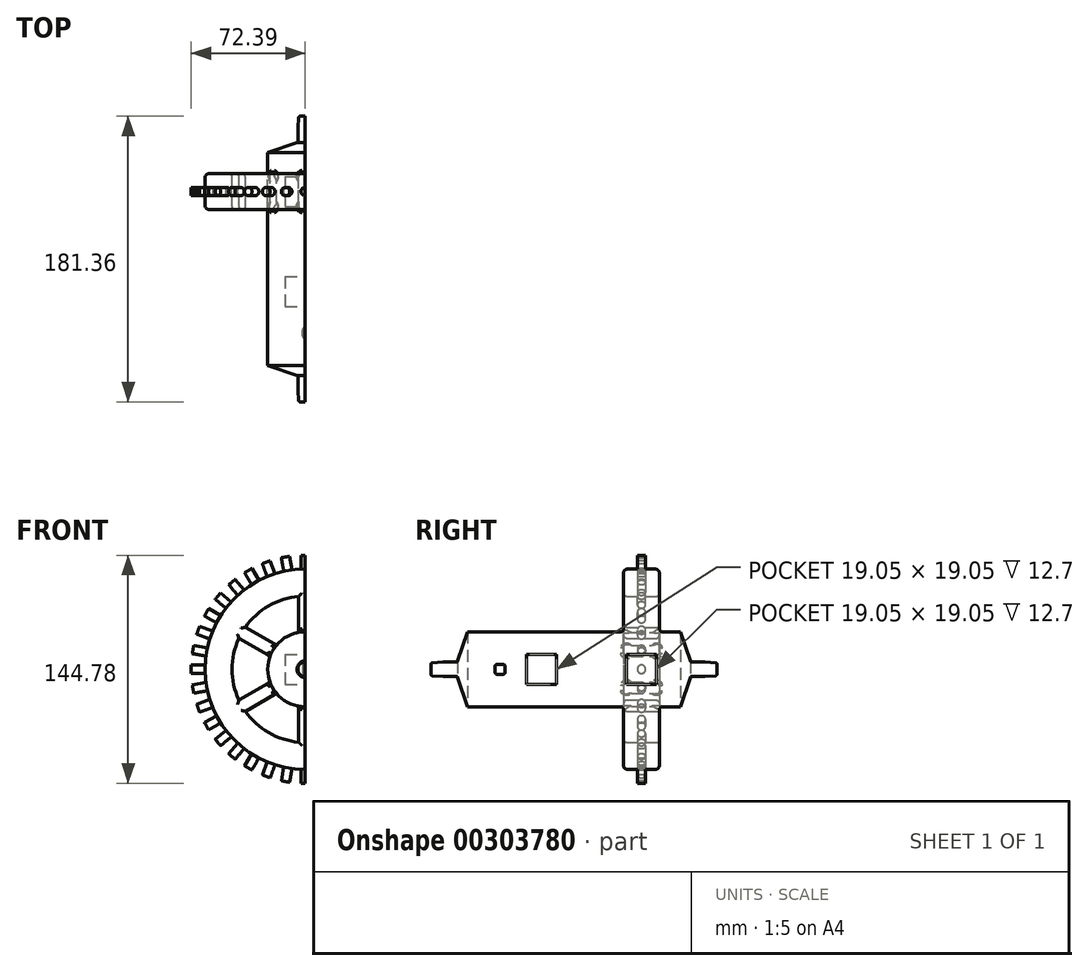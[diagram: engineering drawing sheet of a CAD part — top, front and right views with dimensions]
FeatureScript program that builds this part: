
annotation { "Feature Type Name" : "Feature", "Feature Type Description" : "" }
export const myFeature = defineFeature(function(context is Context, id is Id, definition is map)
    precondition{}
    {
        {
            var Q0;
            Q0=qCreatedBy(makeId("Front.planeOp"),FACE);
            var sketch = newSketch(context, id + "F0", { "sketchPlane" : qUnion([Q0])});
            skCircle(sketch, "E0", {"center": v(0, 0) * mm, "radius": 63.63 * mm});
            skCircle(sketch, "E1", {"center": v(0, 0) * mm, "radius": 46.48 * mm});
            skCircle(sketch, "E2", {"center": v(0, 0) * mm, "radius": 23.81 * mm});
            skCircle(sketch, "E3", {"center": v(0, 0) * mm, "radius": 4.76 * mm});
            skLineSegment(sketch, "E4.bottom", {"start": v(4.1, 47.97) * mm, "end": v(-4.1, 47.97) * mm});
            skLineSegment(sketch, "E4.top", {"start": v(4.1, 21.49) * mm, "end": v(-4.1, 21.49) * mm});
            skLineSegment(sketch, "E4.left", {"start": v(4.1, 47.97) * mm, "end": v(4.1, 21.49) * mm});
            skLineSegment(sketch, "E4.right", {"start": v(-4.1, 47.97) * mm, "end": v(-4.1, 21.49) * mm});
            skPoint(sketch, "E4.middle", {"position": v(0, 34.73) * mm});
            skPoint(sketch, "E5.1.0", {"position": v(30.08, 17.36) * mm});
            skPoint(sketch, "E5.2.0", {"position": v(30.08, -17.36) * mm});
            skLineSegment(sketch, "E5.anchor1", {"start": v(0, 0) * mm, "end": v(0, 34.73) * mm, "construction": true});
            skLineSegment(sketch, "E5.anchor2", {"start": v(0, 0) * mm, "end": v(30.08, -17.36) * mm, "construction": true});
            skLineSegment(sketch, "E6.1.0", {"start": v(43.6, 20.43) * mm, "end": v(20.66, 7.2) * mm});
            skLineSegment(sketch, "E6.2.0", {"start": v(39.5, -27.54) * mm, "end": v(16.56, -14.3) * mm});
            skLineSegment(sketch, "E6.anchor1", {"start": v(0, 0) * mm, "end": v(4.1, 21.49) * mm, "construction": true});
            skLineSegment(sketch, "E6.anchor2", {"start": v(0, 0) * mm, "end": v(16.56, -14.3) * mm, "construction": true});
            skLineSegment(sketch, "E7.1.0", {"start": v(39.5, 27.54) * mm, "end": v(16.56, 14.3) * mm});
            skLineSegment(sketch, "E7.2.0", {"start": v(43.6, -20.43) * mm, "end": v(20.66, -7.2) * mm});
            skLineSegment(sketch, "E7.anchor1", {"start": v(0, 0) * mm, "end": v(-4.1, 21.49) * mm, "construction": true});
            skLineSegment(sketch, "E7.anchor2", {"start": v(0, 0) * mm, "end": v(20.66, -7.2) * mm, "construction": true});
            skLineSegment(sketch, "E8.1.0", {"start": v(20.66, 7.2) * mm, "end": v(16.56, 14.3) * mm});
            skLineSegment(sketch, "E8.2.0", {"start": v(16.56, -14.3) * mm, "end": v(20.66, -7.2) * mm});
            skLineSegment(sketch, "E9.1.0", {"start": v(43.6, 20.43) * mm, "end": v(39.5, 27.54) * mm});
            skLineSegment(sketch, "E9.2.0", {"start": v(39.5, -27.54) * mm, "end": v(43.6, -20.43) * mm});
            skLineSegment(sketch, "E9.anchor1", {"start": v(0, 0) * mm, "end": v(-4.1, 47.97) * mm, "construction": true});
            skLineSegment(sketch, "E9.anchor2", {"start": v(0, 0) * mm, "end": v(43.6, -20.43) * mm, "construction": true});
            skLineSegment(sketch, "E10.bottom", {"start": v(4.1, -19) * mm, "end": v(-4.1, -19) * mm});
            skLineSegment(sketch, "E10.top", {"start": v(4.1, -51.61) * mm, "end": v(-4.1, -51.61) * mm});
            skLineSegment(sketch, "E10.left", {"start": v(4.1, -19) * mm, "end": v(4.1, -51.61) * mm});
            skLineSegment(sketch, "E10.right", {"start": v(-4.1, -19) * mm, "end": v(-4.1, -51.61) * mm});
            skPoint(sketch, "E10.middle", {"position": v(0, -35.3) * mm});
            skLineSegment(sketch, "E11.1.0", {"start": v(-18.5, -5.95) * mm, "end": v(-46.75, -22.25) * mm});
            skLineSegment(sketch, "E11.2.0", {"start": v(-14.4, 13.05) * mm, "end": v(-42.65, 29.36) * mm});
            skLineSegment(sketch, "E11.anchor1", {"start": v(0, 0) * mm, "end": v(-4.1, -51.61) * mm, "construction": true});
            skLineSegment(sketch, "E11.anchor2", {"start": v(0, 0) * mm, "end": v(-42.65, 29.36) * mm, "construction": true});
            skLineSegment(sketch, "E12.1.0", {"start": v(-14.4, -13.05) * mm, "end": v(-42.65, -29.36) * mm});
            skLineSegment(sketch, "E12.2.0", {"start": v(-18.5, 5.95) * mm, "end": v(-46.75, 22.25) * mm});
            skLineSegment(sketch, "E12.anchor1", {"start": v(0, 0) * mm, "end": v(4.1, -51.61) * mm, "construction": true});
            skLineSegment(sketch, "E12.anchor2", {"start": v(0, 0) * mm, "end": v(-46.75, 22.25) * mm, "construction": true});
            skLineSegment(sketch, "E13.1.0", {"start": v(-42.65, -29.36) * mm, "end": v(-46.75, -22.25) * mm});
            skLineSegment(sketch, "E13.1.1", {"start": v(-14.4, -13.05) * mm, "end": v(-18.5, -5.95) * mm});
            skLineSegment(sketch, "E13.2.0", {"start": v(-46.75, 22.25) * mm, "end": v(-42.65, 29.36) * mm});
            skLineSegment(sketch, "E13.2.1", {"start": v(-18.5, 5.95) * mm, "end": v(-14.4, 13.05) * mm});
            skSolve(sketch);
        }
        {
            var Q0;
            Q0=makeQuery(id+"F0.imprint","IMPRINT",FACE,{"disambiguationData":[TD([[makeQuery(id+"F0.imprint","IMPRINT",EDGE,{"derivedFrom":sQuery(id+"F0.wireOp",EDGE,"E0")}),1.0]])]});
            var Q1;
            {var subQ5=sQuery(id+"F0.wireOp",EDGE,"E4.bottom");Q1=makeQuery(id+"F0.imprint","IMPRINT",FACE,{"disambiguationData":[TD([[makeQuery(id+"F0.imprint","IMPRINT",EDGE,{"derivedFrom":subQ5}),1.0]])]});}
            var Q2;
            {var subQ5=sQuery(id+"F0.wireOp",EDGE,"E9.1.0");Q2=makeQuery(id+"F0.imprint","IMPRINT",FACE,{"disambiguationData":[TD([[makeQuery(id+"F0.imprint","IMPRINT",EDGE,{"derivedFrom":subQ5}),1.0]])]});}
            var Q3;
            {var subQ5=sQuery(id+"F0.wireOp",EDGE,"E9.2.0");Q3=makeQuery(id+"F0.imprint","IMPRINT",FACE,{"disambiguationData":[TD([[makeQuery(id+"F0.imprint","IMPRINT",EDGE,{"derivedFrom":subQ5}),1.0]])]});}
            var Q4;
            {var subQ5=sQuery(id+"F0.wireOp",EDGE,"E13.2.0");Q4=makeQuery(id+"F0.imprint","IMPRINT",FACE,{"disambiguationData":[TD([[makeQuery(id+"F0.imprint","IMPRINT",EDGE,{"derivedFrom":subQ5}),-1.0]])]});}
            var Q5;
            {var subQ5=sQuery(id+"F0.wireOp",EDGE,"E13.1.0");Q5=makeQuery(id+"F0.imprint","IMPRINT",FACE,{"disambiguationData":[TD([[makeQuery(id+"F0.imprint","IMPRINT",EDGE,{"derivedFrom":subQ5}),-1.0]])]});}
            var Q6;
            {var subQ5=sQuery(id+"F0.wireOp",EDGE,"E10.top");Q6=makeQuery(id+"F0.imprint","IMPRINT",FACE,{"disambiguationData":[TD([[makeQuery(id+"F0.imprint","IMPRINT",EDGE,{"derivedFrom":subQ5}),-1.0]])]});}
            extrude(context, id + "F1", {"entities" : qUnion([Q0, Q1, Q2, Q3, Q4, Q5, Q6]), "endBound" : BoundingType.SYMMETRIC, "depth" : 22.76 * mm});
        }
        {
            var Q0;
            Q0=makeQuery(id+"F1.opExtrude","CAP_EDGE",EDGE,{"disambiguationData":[OSD([sQuery(id+"F0.wireOp",EDGE,"E0")])],"isStart":false});
            var Q1;
            Q1=makeQuery(id+"F1.opExtrude","CAP_EDGE",EDGE,{"disambiguationData":[OSD([sQuery(id+"F0.wireOp",EDGE,"E0")])],"isStart":true});
            fillet(context, id + "F2", {"entities" : qUnion([Q0, Q1]), "radius" : 2.54 * mm, "tangentPropagation" : true, "allowEdgeOverflow" : false});
        }
        {
            var Q0;
            {var subQ0=sQuery(id+"F0.wireOp",EDGE,"E4.left");var subQ1=sQuery(id+"F0.wireOp",EDGE,"E1");var subQ2=makeQuery(id+"F0.imprint","INTERSECT",VERTEX,{"derivedFrom":[subQ1,subQ0]});Q0=makeQuery(id+"F0.imprint","IMPRINT",FACE,{"disambiguationData":[TD([[makeQuery(id+"F0.imprint","IMPRINT",EDGE,{"disambiguationData":[TD([[subQ2,-1.0]])],"derivedFrom":subQ1}),1.0]])]});}
            var Q1;
            {var subQ0=sQuery(id+"F0.wireOp",EDGE,"E7.1.0");var subQ1=sQuery(id+"F0.wireOp",EDGE,"E1");var subQ2=makeQuery(id+"F0.imprint","INTERSECT",VERTEX,{"derivedFrom":[subQ1,subQ0]});Q1=makeQuery(id+"F0.imprint","IMPRINT",FACE,{"disambiguationData":[TD([[makeQuery(id+"F0.imprint","IMPRINT",EDGE,{"disambiguationData":[TD([[subQ2,1.0]])],"derivedFrom":subQ1}),1.0]])]});}
            var Q2;
            {var subQ0=sQuery(id+"F0.wireOp",EDGE,"E6.2.0");var subQ1=sQuery(id+"F0.wireOp",EDGE,"E1");var subQ2=makeQuery(id+"F0.imprint","INTERSECT",VERTEX,{"derivedFrom":[subQ1,subQ0]});Q2=makeQuery(id+"F0.imprint","IMPRINT",FACE,{"disambiguationData":[TD([[makeQuery(id+"F0.imprint","IMPRINT",EDGE,{"disambiguationData":[TD([[subQ2,-1.0]])],"derivedFrom":subQ1}),1.0]])]});}
            var Q3;
            {var subQ0=sQuery(id+"F0.wireOp",EDGE,"E11.2.0");var subQ1=sQuery(id+"F0.wireOp",EDGE,"E1");var subQ2=makeQuery(id+"F0.imprint","INTERSECT",VERTEX,{"derivedFrom":[subQ1,subQ0]});Q3=makeQuery(id+"F0.imprint","IMPRINT",FACE,{"disambiguationData":[TD([[makeQuery(id+"F0.imprint","IMPRINT",EDGE,{"disambiguationData":[TD([[subQ2,-1.0]])],"derivedFrom":subQ1}),1.0]])]});}
            var Q4;
            {var subQ0=sQuery(id+"F0.wireOp",EDGE,"E11.1.0");var subQ1=sQuery(id+"F0.wireOp",EDGE,"E1");var subQ2=makeQuery(id+"F0.imprint","INTERSECT",VERTEX,{"derivedFrom":[subQ1,subQ0]});Q4=makeQuery(id+"F0.imprint","IMPRINT",FACE,{"disambiguationData":[TD([[makeQuery(id+"F0.imprint","IMPRINT",EDGE,{"disambiguationData":[TD([[subQ2,-1.0]])],"derivedFrom":subQ1}),1.0]])]});}
            var Q5;
            {var subQ0=sQuery(id+"F0.wireOp",EDGE,"E10.right");var subQ1=sQuery(id+"F0.wireOp",EDGE,"E1");var subQ2=makeQuery(id+"F0.imprint","INTERSECT",VERTEX,{"derivedFrom":[subQ1,subQ0]});Q5=makeQuery(id+"F0.imprint","IMPRINT",FACE,{"disambiguationData":[TD([[makeQuery(id+"F0.imprint","IMPRINT",EDGE,{"disambiguationData":[TD([[subQ2,-1.0]])],"derivedFrom":subQ1}),1.0]])]});}
            extrude(context, id + "F3", {"entities" : qUnion([Q0, Q1, Q2, Q3, Q4, Q5]), "operationType" : NewBodyOperationType.ADD, "endBound" : BoundingType.SYMMETRIC, "depth" : 22.76 * mm});
        }
        {
            var Q0;
            Q0=makeQuery(id+"F0.imprint","IMPRINT",FACE,{"disambiguationData":[TD([[makeQuery(id+"F0.imprint","IMPRINT",EDGE,{"derivedFrom":sQuery(id+"F0.wireOp",EDGE,"E3")}),-1.0]])]});
            var Q1;
            Q1=makeQuery(id+"F0.imprint","IMPRINT",FACE,{"disambiguationData":[TD([[makeQuery(id+"F0.imprint","IMPRINT",EDGE,{"derivedFrom":sQuery(id+"F0.wireOp",EDGE,"E3")}),1.0]])]});
            var Q2;
            {var subQ5=sQuery(id+"F0.wireOp",EDGE,"E13.1.1");Q2=makeQuery(id+"F0.imprint","IMPRINT",FACE,{"disambiguationData":[TD([[makeQuery(id+"F0.imprint","IMPRINT",EDGE,{"derivedFrom":subQ5}),1.0]])]});}
            var Q3;
            {var subQ5=sQuery(id+"F0.wireOp",EDGE,"E13.2.1");Q3=makeQuery(id+"F0.imprint","IMPRINT",FACE,{"disambiguationData":[TD([[makeQuery(id+"F0.imprint","IMPRINT",EDGE,{"derivedFrom":subQ5}),1.0]])]});}
            var Q4;
            {var subQ5=sQuery(id+"F0.wireOp",EDGE,"E4.top");Q4=makeQuery(id+"F0.imprint","IMPRINT",FACE,{"disambiguationData":[TD([[makeQuery(id+"F0.imprint","IMPRINT",EDGE,{"derivedFrom":subQ5}),-1.0]])]});}
            var Q5;
            {var subQ5=sQuery(id+"F0.wireOp",EDGE,"E8.1.0");Q5=makeQuery(id+"F0.imprint","IMPRINT",FACE,{"disambiguationData":[TD([[makeQuery(id+"F0.imprint","IMPRINT",EDGE,{"derivedFrom":subQ5}),-1.0]])]});}
            var Q6;
            {var subQ5=sQuery(id+"F0.wireOp",EDGE,"E8.2.0");Q6=makeQuery(id+"F0.imprint","IMPRINT",FACE,{"disambiguationData":[TD([[makeQuery(id+"F0.imprint","IMPRINT",EDGE,{"derivedFrom":subQ5}),-1.0]])]});}
            var Q7;
            {var subQ5=sQuery(id+"F0.wireOp",EDGE,"E10.bottom");Q7=makeQuery(id+"F0.imprint","IMPRINT",FACE,{"disambiguationData":[TD([[makeQuery(id+"F0.imprint","IMPRINT",EDGE,{"derivedFrom":subQ5}),1.0]])]});}
            extrude(context, id + "F4", {"entities" : qUnion([Q0, Q1, Q2, Q3, Q4, Q5, Q6, Q7]), "operationType" : NewBodyOperationType.ADD, "depth" : 116.78 * mm});
        }
        {
            var Q0;
            Q0=makeQuery(id+"F0.imprint","IMPRINT",FACE,{"disambiguationData":[TD([[makeQuery(id+"F0.imprint","IMPRINT",EDGE,{"derivedFrom":sQuery(id+"F0.wireOp",EDGE,"E3")}),-1.0]])]});
            var Q1;
            {var subQ5=sQuery(id+"F0.wireOp",EDGE,"E8.1.0");Q1=makeQuery(id+"F0.imprint","IMPRINT",FACE,{"disambiguationData":[TD([[makeQuery(id+"F0.imprint","IMPRINT",EDGE,{"derivedFrom":subQ5}),-1.0]])]});}
            var Q2;
            {var subQ5=sQuery(id+"F0.wireOp",EDGE,"E4.top");Q2=makeQuery(id+"F0.imprint","IMPRINT",FACE,{"disambiguationData":[TD([[makeQuery(id+"F0.imprint","IMPRINT",EDGE,{"derivedFrom":subQ5}),-1.0]])]});}
            var Q3;
            {var subQ5=sQuery(id+"F0.wireOp",EDGE,"E13.2.1");Q3=makeQuery(id+"F0.imprint","IMPRINT",FACE,{"disambiguationData":[TD([[makeQuery(id+"F0.imprint","IMPRINT",EDGE,{"derivedFrom":subQ5}),1.0]])]});}
            var Q4;
            {var subQ5=sQuery(id+"F0.wireOp",EDGE,"E13.1.1");Q4=makeQuery(id+"F0.imprint","IMPRINT",FACE,{"disambiguationData":[TD([[makeQuery(id+"F0.imprint","IMPRINT",EDGE,{"derivedFrom":subQ5}),1.0]])]});}
            var Q5;
            {var subQ5=sQuery(id+"F0.wireOp",EDGE,"E10.bottom");Q5=makeQuery(id+"F0.imprint","IMPRINT",FACE,{"disambiguationData":[TD([[makeQuery(id+"F0.imprint","IMPRINT",EDGE,{"derivedFrom":subQ5}),1.0]])]});}
            var Q6;
            {var subQ5=sQuery(id+"F0.wireOp",EDGE,"E8.2.0");Q6=makeQuery(id+"F0.imprint","IMPRINT",FACE,{"disambiguationData":[TD([[makeQuery(id+"F0.imprint","IMPRINT",EDGE,{"derivedFrom":subQ5}),-1.0]])]});}
            var Q7;
            Q7=makeQuery(id+"F0.imprint","IMPRINT",FACE,{"disambiguationData":[TD([[makeQuery(id+"F0.imprint","IMPRINT",EDGE,{"derivedFrom":sQuery(id+"F0.wireOp",EDGE,"E3")}),1.0]])]});
            extrude(context, id + "F5", {"entities" : qUnion([Q0, Q1, Q2, Q3, Q4, Q5, Q6, Q7]), "operationType" : NewBodyOperationType.ADD, "oppositeDirection" : true, "depth" : 31.05 * mm});
        }
        {
            var Q0;
            Q0=makeQuery(id+"F5.opExtrude","CAP_FACE",FACE,{"disambiguationData":[OSD([sQuery(id+"F0.wireOp",EDGE,"E2")])],"isStart":false});
            var sketch = newSketch(context, id + "F6", { "sketchPlane" : qUnion([Q0])});
            skCircle(sketch, "E14", {"center": v(0, 0) * mm, "radius": 4.7 * mm});
            skSolve(sketch);
        }
        {
            var Q0;
            Q0=makeQuery(id+"F6.imprint","IMPRINT",FACE,{"disambiguationData":[TD([[makeQuery(id+"F6.imprint","IMPRINT",EDGE,{"derivedFrom":sQuery(id+"F6.wireOp",EDGE,"E14")}),1.0]])]});
            extrude(context, id + "F7", {"entities" : qUnion([Q0]), "operationType" : NewBodyOperationType.ADD, "depth" : 16.76 * mm});
        }
        {
            var Q0;
            Q0=makeQuery(id+"F4.opExtrude","CAP_FACE",FACE,{"disambiguationData":[OSD([sQuery(id+"F0.wireOp",EDGE,"E2")])],"isStart":false});
            var sketch = newSketch(context, id + "F8", { "sketchPlane" : qUnion([Q0])});
            skCircle(sketch, "E15", {"center": v(0, 0) * mm, "radius": 4.7 * mm});
            skSolve(sketch);
        }
        {
            var Q0;
            Q0 = qSketchRegion(id + "F8", true);
            extrude(context, id + "F9", {"entities" : qUnion([Q0]), "operationType" : NewBodyOperationType.ADD, "depth" : 16.76 * mm});
        }
        {
            var Q0;
            {var subQ0=sQuery(id+"F0.wireOp",EDGE,"E2");var subQ1=sQuery(id+"F0.wireOp",EDGE,"E1");Q0=makeQuery(id+"F3.boolean.opBoolean","MERGE",FACE,{"derivedFrom":[makeQuery(id+"F1.opExtrude","CAP_FACE",FACE,{"disambiguationData":[OSD([sQuery(id+"F0.wireOp",EDGE,"E0"),subQ1])],"isStart":false}),makeQuery(id+"F3.opExtrude","CAP_FACE",FACE,{"disambiguationData":[OSD([subQ1,subQ0,sQuery(id+"F0.wireOp",EDGE,"E6.1.0"),sQuery(id+"F0.wireOp",EDGE,"E7.1.0")])],"isStart":false}),makeQuery(id+"F3.opExtrude","CAP_FACE",FACE,{"disambiguationData":[OSD([subQ1,subQ0,sQuery(id+"F0.wireOp",EDGE,"E4.left"),sQuery(id+"F0.wireOp",EDGE,"E4.right")])],"isStart":false}),makeQuery(id+"F3.opExtrude","CAP_FACE",FACE,{"disambiguationData":[OSD([subQ1,subQ0,sQuery(id+"F0.wireOp",EDGE,"E11.2.0"),sQuery(id+"F0.wireOp",EDGE,"E12.2.0")])],"isStart":false}),makeQuery(id+"F3.opExtrude","CAP_FACE",FACE,{"disambiguationData":[OSD([subQ1,subQ0,sQuery(id+"F0.wireOp",EDGE,"E11.1.0"),sQuery(id+"F0.wireOp",EDGE,"E12.1.0")])],"isStart":false}),makeQuery(id+"F3.opExtrude","CAP_FACE",FACE,{"disambiguationData":[OSD([subQ1,subQ0,sQuery(id+"F0.wireOp",EDGE,"E10.left"),sQuery(id+"F0.wireOp",EDGE,"E10.right")])],"isStart":false}),makeQuery(id+"F3.opExtrude","CAP_FACE",FACE,{"disambiguationData":[OSD([subQ1,subQ0,sQuery(id+"F0.wireOp",EDGE,"E6.2.0"),sQuery(id+"F0.wireOp",EDGE,"E7.2.0")])],"isStart":false})]});}
            var Q1;
            {var subQ0=sQuery(id+"F0.wireOp",EDGE,"E2");var subQ1=sQuery(id+"F0.wireOp",EDGE,"E1");Q1=makeQuery(id+"F4.boolean.opBoolean","MERGE",FACE,{"derivedFrom":[makeQuery(id+"F3.boolean.opBoolean","MERGE",FACE,{"derivedFrom":[makeQuery(id+"F1.opExtrude","CAP_FACE",FACE,{"disambiguationData":[OSD([sQuery(id+"F0.wireOp",EDGE,"E0"),subQ1])],"isStart":true}),makeQuery(id+"F3.opExtrude","CAP_FACE",FACE,{"disambiguationData":[OSD([subQ1,subQ0,sQuery(id+"F0.wireOp",EDGE,"E6.1.0"),sQuery(id+"F0.wireOp",EDGE,"E7.1.0")])],"isStart":true}),makeQuery(id+"F3.opExtrude","CAP_FACE",FACE,{"disambiguationData":[OSD([subQ1,subQ0,sQuery(id+"F0.wireOp",EDGE,"E4.left"),sQuery(id+"F0.wireOp",EDGE,"E4.right")])],"isStart":true}),makeQuery(id+"F3.opExtrude","CAP_FACE",FACE,{"disambiguationData":[OSD([subQ1,subQ0,sQuery(id+"F0.wireOp",EDGE,"E11.2.0"),sQuery(id+"F0.wireOp",EDGE,"E12.2.0")])],"isStart":true}),makeQuery(id+"F3.opExtrude","CAP_FACE",FACE,{"disambiguationData":[OSD([subQ1,subQ0,sQuery(id+"F0.wireOp",EDGE,"E11.1.0"),sQuery(id+"F0.wireOp",EDGE,"E12.1.0")])],"isStart":true}),makeQuery(id+"F3.opExtrude","CAP_FACE",FACE,{"disambiguationData":[OSD([subQ1,subQ0,sQuery(id+"F0.wireOp",EDGE,"E10.left"),sQuery(id+"F0.wireOp",EDGE,"E10.right")])],"isStart":true}),makeQuery(id+"F3.opExtrude","CAP_FACE",FACE,{"disambiguationData":[OSD([subQ1,subQ0,sQuery(id+"F0.wireOp",EDGE,"E6.2.0"),sQuery(id+"F0.wireOp",EDGE,"E7.2.0")])],"isStart":true})]}),makeQuery(id+"F4.opExtrude","CAP_FACE",FACE,{"disambiguationData":[OSD([subQ0])],"isStart":true})]});}
            fillet(context, id + "F10", {"entities" : qUnion([Q0, Q1]), "radius" : 1.9 * mm, "tangentPropagation" : true, "allowEdgeOverflow" : false});
        }
        {
            var Q0;
            Q0=makeQuery(id+"F4.opExtrude","CAP_EDGE",EDGE,{"disambiguationData":[OSD([sQuery(id+"F0.wireOp",EDGE,"E2")])],"isStart":false});
            var Q1;
            Q1=makeQuery(id+"F5.opExtrude","CAP_EDGE",EDGE,{"disambiguationData":[OSD([sQuery(id+"F0.wireOp",EDGE,"E2")])],"isStart":false});
            chamfer(context, id + "F11", {"entities" : qUnion([Q0, Q1]), "chamferType" : ChamferType.TWO_OFFSETS, "width1" : 18.55 * mm, "oppositeDirection" : false, "width2" : 6.35 * mm, "tangentPropagation" : true});
        }
        {
            var Q0;
            Q0=qCreatedBy(makeId("Front.planeOp"),FACE);
            var sketch = newSketch(context, id + "F12", { "sketchPlane" : qUnion([Q0])});
            skLineSegment(sketch, "E16.bottom", {"start": v(2.67, 61.09) * mm, "end": v(-2.67, 61.09) * mm});
            skLineSegment(sketch, "E16.top", {"start": v(2.67, 72.4) * mm, "end": v(-2.67, 72.4) * mm});
            skLineSegment(sketch, "E16.left", {"start": v(2.67, 61.09) * mm, "end": v(2.67, 72.4) * mm});
            skLineSegment(sketch, "E16.right", {"start": v(-2.67, 61.09) * mm, "end": v(-2.67, 72.4) * mm});
            skPoint(sketch, "E16.middle", {"position": v(0, 66.74) * mm});
            skLineSegment(sketch, "E17.1.0", {"start": v(7.98, 60.62) * mm, "end": v(9.94, 71.75) * mm});
            skLineSegment(sketch, "E17.1.1", {"start": v(15.2, 70.83) * mm, "end": v(9.94, 71.75) * mm});
            skLineSegment(sketch, "E17.1.2", {"start": v(13.23, 59.7) * mm, "end": v(15.2, 70.83) * mm});
            skLineSegment(sketch, "E17.1.3", {"start": v(13.23, 59.7) * mm, "end": v(7.98, 60.62) * mm});
            skLineSegment(sketch, "E17.2.0", {"start": v(18.39, 58.32) * mm, "end": v(22.25, 68.94) * mm});
            skLineSegment(sketch, "E17.2.1", {"start": v(27.26, 67.11) * mm, "end": v(22.25, 68.94) * mm});
            skLineSegment(sketch, "E17.2.2", {"start": v(23.4, 56.5) * mm, "end": v(27.26, 67.11) * mm});
            skLineSegment(sketch, "E17.2.3", {"start": v(23.4, 56.5) * mm, "end": v(18.39, 58.32) * mm});
            skLineSegment(sketch, "E17.3.0", {"start": v(28.23, 54.24) * mm, "end": v(33.89, 64.03) * mm});
            skLineSegment(sketch, "E17.3.1", {"start": v(38.5, 61.36) * mm, "end": v(33.89, 64.03) * mm});
            skLineSegment(sketch, "E17.3.2", {"start": v(32.85, 51.57) * mm, "end": v(38.5, 61.36) * mm});
            skLineSegment(sketch, "E17.3.3", {"start": v(32.85, 51.57) * mm, "end": v(28.23, 54.24) * mm});
            skLineSegment(sketch, "E17.4.0", {"start": v(37.22, 48.5) * mm, "end": v(44.49, 57.17) * mm});
            skLineSegment(sketch, "E17.4.1", {"start": v(48.57, 53.74) * mm, "end": v(44.49, 57.17) * mm});
            skLineSegment(sketch, "E17.4.2", {"start": v(41.3, 45.08) * mm, "end": v(48.57, 53.74) * mm});
            skLineSegment(sketch, "E17.4.3", {"start": v(41.3, 45.08) * mm, "end": v(37.22, 48.5) * mm});
            skLineSegment(sketch, "E17.5.0", {"start": v(45.08, 41.3) * mm, "end": v(53.74, 48.57) * mm});
            skLineSegment(sketch, "E17.5.1", {"start": v(57.17, 44.49) * mm, "end": v(53.74, 48.57) * mm});
            skLineSegment(sketch, "E17.5.2", {"start": v(48.5, 37.22) * mm, "end": v(57.17, 44.49) * mm});
            skLineSegment(sketch, "E17.5.3", {"start": v(48.5, 37.22) * mm, "end": v(45.08, 41.3) * mm});
            skLineSegment(sketch, "E17.6.0", {"start": v(51.57, 32.85) * mm, "end": v(61.36, 38.5) * mm});
            skLineSegment(sketch, "E17.6.1", {"start": v(64.03, 33.89) * mm, "end": v(61.36, 38.5) * mm});
            skLineSegment(sketch, "E17.6.2", {"start": v(54.24, 28.23) * mm, "end": v(64.03, 33.89) * mm});
            skLineSegment(sketch, "E17.6.3", {"start": v(54.24, 28.23) * mm, "end": v(51.57, 32.85) * mm});
            skLineSegment(sketch, "E17.7.0", {"start": v(56.5, 23.4) * mm, "end": v(67.11, 27.26) * mm});
            skLineSegment(sketch, "E17.7.1", {"start": v(68.94, 22.25) * mm, "end": v(67.11, 27.26) * mm});
            skLineSegment(sketch, "E17.7.2", {"start": v(58.32, 18.39) * mm, "end": v(68.94, 22.25) * mm});
            skLineSegment(sketch, "E17.7.3", {"start": v(58.32, 18.39) * mm, "end": v(56.5, 23.4) * mm});
            skLineSegment(sketch, "E17.8.0", {"start": v(59.7, 13.23) * mm, "end": v(70.83, 15.2) * mm});
            skLineSegment(sketch, "E17.8.1", {"start": v(71.75, 9.94) * mm, "end": v(70.83, 15.2) * mm});
            skLineSegment(sketch, "E17.8.2", {"start": v(60.62, 7.98) * mm, "end": v(71.75, 9.94) * mm});
            skLineSegment(sketch, "E17.8.3", {"start": v(60.62, 7.98) * mm, "end": v(59.7, 13.23) * mm});
            skLineSegment(sketch, "E17.9.0", {"start": v(61.09, 2.67) * mm, "end": v(72.4, 2.67) * mm});
            skLineSegment(sketch, "E17.9.1", {"start": v(72.4, -2.67) * mm, "end": v(72.4, 2.67) * mm});
            skLineSegment(sketch, "E17.9.2", {"start": v(61.09, -2.67) * mm, "end": v(72.4, -2.67) * mm});
            skLineSegment(sketch, "E17.9.3", {"start": v(61.09, -2.67) * mm, "end": v(61.09, 2.67) * mm});
            skLineSegment(sketch, "E17.10.0", {"start": v(60.62, -7.98) * mm, "end": v(71.75, -9.94) * mm});
            skLineSegment(sketch, "E17.10.1", {"start": v(70.83, -15.2) * mm, "end": v(71.75, -9.94) * mm});
            skLineSegment(sketch, "E17.10.2", {"start": v(59.7, -13.23) * mm, "end": v(70.83, -15.2) * mm});
            skLineSegment(sketch, "E17.10.3", {"start": v(59.7, -13.23) * mm, "end": v(60.62, -7.98) * mm});
            skLineSegment(sketch, "E17.11.0", {"start": v(58.32, -18.39) * mm, "end": v(68.94, -22.25) * mm});
            skLineSegment(sketch, "E17.11.1", {"start": v(67.11, -27.26) * mm, "end": v(68.94, -22.25) * mm});
            skLineSegment(sketch, "E17.11.2", {"start": v(56.5, -23.4) * mm, "end": v(67.11, -27.26) * mm});
            skLineSegment(sketch, "E17.11.3", {"start": v(56.5, -23.4) * mm, "end": v(58.32, -18.39) * mm});
            skLineSegment(sketch, "E17.12.0", {"start": v(54.24, -28.23) * mm, "end": v(64.03, -33.89) * mm});
            skLineSegment(sketch, "E17.12.1", {"start": v(61.36, -38.5) * mm, "end": v(64.03, -33.89) * mm});
            skLineSegment(sketch, "E17.12.2", {"start": v(51.57, -32.85) * mm, "end": v(61.36, -38.5) * mm});
            skLineSegment(sketch, "E17.12.3", {"start": v(51.57, -32.85) * mm, "end": v(54.24, -28.23) * mm});
            skLineSegment(sketch, "E17.13.0", {"start": v(48.5, -37.22) * mm, "end": v(57.17, -44.49) * mm});
            skLineSegment(sketch, "E17.13.1", {"start": v(53.74, -48.57) * mm, "end": v(57.17, -44.49) * mm});
            skLineSegment(sketch, "E17.13.2", {"start": v(45.08, -41.3) * mm, "end": v(53.74, -48.57) * mm});
            skLineSegment(sketch, "E17.13.3", {"start": v(45.08, -41.3) * mm, "end": v(48.5, -37.22) * mm});
            skLineSegment(sketch, "E17.14.0", {"start": v(41.3, -45.08) * mm, "end": v(48.57, -53.74) * mm});
            skLineSegment(sketch, "E17.14.1", {"start": v(44.49, -57.17) * mm, "end": v(48.57, -53.74) * mm});
            skLineSegment(sketch, "E17.14.2", {"start": v(37.22, -48.5) * mm, "end": v(44.49, -57.17) * mm});
            skLineSegment(sketch, "E17.14.3", {"start": v(37.22, -48.5) * mm, "end": v(41.3, -45.08) * mm});
            skLineSegment(sketch, "E17.15.0", {"start": v(32.85, -51.57) * mm, "end": v(38.5, -61.36) * mm});
            skLineSegment(sketch, "E17.15.1", {"start": v(33.89, -64.03) * mm, "end": v(38.5, -61.36) * mm});
            skLineSegment(sketch, "E17.15.2", {"start": v(28.23, -54.24) * mm, "end": v(33.89, -64.03) * mm});
            skLineSegment(sketch, "E17.15.3", {"start": v(28.23, -54.24) * mm, "end": v(32.85, -51.57) * mm});
            skLineSegment(sketch, "E17.16.0", {"start": v(23.4, -56.5) * mm, "end": v(27.26, -67.11) * mm});
            skLineSegment(sketch, "E17.16.1", {"start": v(22.25, -68.94) * mm, "end": v(27.26, -67.11) * mm});
            skLineSegment(sketch, "E17.16.2", {"start": v(18.39, -58.32) * mm, "end": v(22.25, -68.94) * mm});
            skLineSegment(sketch, "E17.16.3", {"start": v(18.39, -58.32) * mm, "end": v(23.4, -56.5) * mm});
            skLineSegment(sketch, "E17.17.0", {"start": v(13.23, -59.7) * mm, "end": v(15.2, -70.83) * mm});
            skLineSegment(sketch, "E17.17.1", {"start": v(9.94, -71.75) * mm, "end": v(15.2, -70.83) * mm});
            skLineSegment(sketch, "E17.17.2", {"start": v(7.98, -60.62) * mm, "end": v(9.94, -71.75) * mm});
            skLineSegment(sketch, "E17.17.3", {"start": v(7.98, -60.62) * mm, "end": v(13.23, -59.7) * mm});
            skLineSegment(sketch, "E17.18.0", {"start": v(2.67, -61.09) * mm, "end": v(2.67, -72.4) * mm});
            skLineSegment(sketch, "E17.18.1", {"start": v(-2.67, -72.4) * mm, "end": v(2.67, -72.4) * mm});
            skLineSegment(sketch, "E17.18.2", {"start": v(-2.67, -61.09) * mm, "end": v(-2.67, -72.4) * mm});
            skLineSegment(sketch, "E17.18.3", {"start": v(-2.67, -61.09) * mm, "end": v(2.67, -61.09) * mm});
            skLineSegment(sketch, "E17.19.0", {"start": v(-7.98, -60.62) * mm, "end": v(-9.94, -71.75) * mm});
            skLineSegment(sketch, "E17.19.1", {"start": v(-15.2, -70.83) * mm, "end": v(-9.94, -71.75) * mm});
            skLineSegment(sketch, "E17.19.2", {"start": v(-13.23, -59.7) * mm, "end": v(-15.2, -70.83) * mm});
            skLineSegment(sketch, "E17.19.3", {"start": v(-13.23, -59.7) * mm, "end": v(-7.98, -60.62) * mm});
            skLineSegment(sketch, "E17.20.0", {"start": v(-18.39, -58.32) * mm, "end": v(-22.25, -68.94) * mm});
            skLineSegment(sketch, "E17.20.1", {"start": v(-27.26, -67.11) * mm, "end": v(-22.25, -68.94) * mm});
            skLineSegment(sketch, "E17.20.2", {"start": v(-23.4, -56.5) * mm, "end": v(-27.26, -67.11) * mm});
            skLineSegment(sketch, "E17.20.3", {"start": v(-23.4, -56.5) * mm, "end": v(-18.39, -58.32) * mm});
            skLineSegment(sketch, "E17.21.0", {"start": v(-28.23, -54.24) * mm, "end": v(-33.89, -64.03) * mm});
            skLineSegment(sketch, "E17.21.1", {"start": v(-38.5, -61.36) * mm, "end": v(-33.89, -64.03) * mm});
            skLineSegment(sketch, "E17.21.2", {"start": v(-32.85, -51.57) * mm, "end": v(-38.5, -61.36) * mm});
            skLineSegment(sketch, "E17.21.3", {"start": v(-32.85, -51.57) * mm, "end": v(-28.23, -54.24) * mm});
            skLineSegment(sketch, "E17.22.0", {"start": v(-37.22, -48.5) * mm, "end": v(-44.49, -57.17) * mm});
            skLineSegment(sketch, "E17.22.1", {"start": v(-48.57, -53.74) * mm, "end": v(-44.49, -57.17) * mm});
            skLineSegment(sketch, "E17.22.2", {"start": v(-41.3, -45.08) * mm, "end": v(-48.57, -53.74) * mm});
            skLineSegment(sketch, "E17.22.3", {"start": v(-41.3, -45.08) * mm, "end": v(-37.22, -48.5) * mm});
            skLineSegment(sketch, "E17.23.0", {"start": v(-45.08, -41.3) * mm, "end": v(-53.74, -48.57) * mm});
            skLineSegment(sketch, "E17.23.1", {"start": v(-57.17, -44.49) * mm, "end": v(-53.74, -48.57) * mm});
            skLineSegment(sketch, "E17.23.2", {"start": v(-48.5, -37.22) * mm, "end": v(-57.17, -44.49) * mm});
            skLineSegment(sketch, "E17.23.3", {"start": v(-48.5, -37.22) * mm, "end": v(-45.08, -41.3) * mm});
            skLineSegment(sketch, "E17.24.0", {"start": v(-51.57, -32.85) * mm, "end": v(-61.36, -38.5) * mm});
            skLineSegment(sketch, "E17.24.1", {"start": v(-64.03, -33.89) * mm, "end": v(-61.36, -38.5) * mm});
            skLineSegment(sketch, "E17.24.2", {"start": v(-54.24, -28.23) * mm, "end": v(-64.03, -33.89) * mm});
            skLineSegment(sketch, "E17.24.3", {"start": v(-54.24, -28.23) * mm, "end": v(-51.57, -32.85) * mm});
            skLineSegment(sketch, "E17.25.0", {"start": v(-56.5, -23.4) * mm, "end": v(-67.11, -27.26) * mm});
            skLineSegment(sketch, "E17.25.1", {"start": v(-68.94, -22.25) * mm, "end": v(-67.11, -27.26) * mm});
            skLineSegment(sketch, "E17.25.2", {"start": v(-58.32, -18.39) * mm, "end": v(-68.94, -22.25) * mm});
            skLineSegment(sketch, "E17.25.3", {"start": v(-58.32, -18.39) * mm, "end": v(-56.5, -23.4) * mm});
            skLineSegment(sketch, "E17.26.0", {"start": v(-59.7, -13.23) * mm, "end": v(-70.83, -15.2) * mm});
            skLineSegment(sketch, "E17.26.1", {"start": v(-71.75, -9.94) * mm, "end": v(-70.83, -15.2) * mm});
            skLineSegment(sketch, "E17.26.2", {"start": v(-60.62, -7.98) * mm, "end": v(-71.75, -9.94) * mm});
            skLineSegment(sketch, "E17.26.3", {"start": v(-60.62, -7.98) * mm, "end": v(-59.7, -13.23) * mm});
            skLineSegment(sketch, "E17.27.0", {"start": v(-61.09, -2.67) * mm, "end": v(-72.4, -2.67) * mm});
            skLineSegment(sketch, "E17.27.1", {"start": v(-72.4, 2.67) * mm, "end": v(-72.4, -2.67) * mm});
            skLineSegment(sketch, "E17.27.2", {"start": v(-61.09, 2.67) * mm, "end": v(-72.4, 2.67) * mm});
            skLineSegment(sketch, "E17.27.3", {"start": v(-61.09, 2.67) * mm, "end": v(-61.09, -2.67) * mm});
            skLineSegment(sketch, "E17.28.0", {"start": v(-60.62, 7.98) * mm, "end": v(-71.75, 9.94) * mm});
            skLineSegment(sketch, "E17.28.1", {"start": v(-70.83, 15.2) * mm, "end": v(-71.75, 9.94) * mm});
            skLineSegment(sketch, "E17.28.2", {"start": v(-59.7, 13.23) * mm, "end": v(-70.83, 15.2) * mm});
            skLineSegment(sketch, "E17.28.3", {"start": v(-59.7, 13.23) * mm, "end": v(-60.62, 7.98) * mm});
            skLineSegment(sketch, "E17.29.0", {"start": v(-58.32, 18.39) * mm, "end": v(-68.94, 22.25) * mm});
            skLineSegment(sketch, "E17.29.1", {"start": v(-67.11, 27.26) * mm, "end": v(-68.94, 22.25) * mm});
            skLineSegment(sketch, "E17.29.2", {"start": v(-56.5, 23.4) * mm, "end": v(-67.11, 27.26) * mm});
            skLineSegment(sketch, "E17.29.3", {"start": v(-56.5, 23.4) * mm, "end": v(-58.32, 18.39) * mm});
            skLineSegment(sketch, "E17.30.0", {"start": v(-54.24, 28.23) * mm, "end": v(-64.03, 33.89) * mm});
            skLineSegment(sketch, "E17.30.1", {"start": v(-61.36, 38.5) * mm, "end": v(-64.03, 33.89) * mm});
            skLineSegment(sketch, "E17.30.2", {"start": v(-51.57, 32.85) * mm, "end": v(-61.36, 38.5) * mm});
            skLineSegment(sketch, "E17.30.3", {"start": v(-51.57, 32.85) * mm, "end": v(-54.24, 28.23) * mm});
            skLineSegment(sketch, "E17.31.0", {"start": v(-48.5, 37.22) * mm, "end": v(-57.17, 44.49) * mm});
            skLineSegment(sketch, "E17.31.1", {"start": v(-53.74, 48.57) * mm, "end": v(-57.17, 44.49) * mm});
            skLineSegment(sketch, "E17.31.2", {"start": v(-45.08, 41.3) * mm, "end": v(-53.74, 48.57) * mm});
            skLineSegment(sketch, "E17.31.3", {"start": v(-45.08, 41.3) * mm, "end": v(-48.5, 37.22) * mm});
            skLineSegment(sketch, "E17.32.0", {"start": v(-41.3, 45.08) * mm, "end": v(-48.57, 53.74) * mm});
            skLineSegment(sketch, "E17.32.1", {"start": v(-44.49, 57.17) * mm, "end": v(-48.57, 53.74) * mm});
            skLineSegment(sketch, "E17.32.2", {"start": v(-37.22, 48.5) * mm, "end": v(-44.49, 57.17) * mm});
            skLineSegment(sketch, "E17.32.3", {"start": v(-37.22, 48.5) * mm, "end": v(-41.3, 45.08) * mm});
            skLineSegment(sketch, "E17.33.0", {"start": v(-32.85, 51.57) * mm, "end": v(-38.5, 61.36) * mm});
            skLineSegment(sketch, "E17.33.1", {"start": v(-33.89, 64.03) * mm, "end": v(-38.5, 61.36) * mm});
            skLineSegment(sketch, "E17.33.2", {"start": v(-28.23, 54.24) * mm, "end": v(-33.89, 64.03) * mm});
            skLineSegment(sketch, "E17.33.3", {"start": v(-28.23, 54.24) * mm, "end": v(-32.85, 51.57) * mm});
            skLineSegment(sketch, "E17.34.0", {"start": v(-23.4, 56.5) * mm, "end": v(-27.26, 67.11) * mm});
            skLineSegment(sketch, "E17.34.1", {"start": v(-22.25, 68.94) * mm, "end": v(-27.26, 67.11) * mm});
            skLineSegment(sketch, "E17.34.2", {"start": v(-18.39, 58.32) * mm, "end": v(-22.25, 68.94) * mm});
            skLineSegment(sketch, "E17.34.3", {"start": v(-18.39, 58.32) * mm, "end": v(-23.4, 56.5) * mm});
            skLineSegment(sketch, "E17.35.0", {"start": v(-13.23, 59.7) * mm, "end": v(-15.2, 70.83) * mm});
            skLineSegment(sketch, "E17.35.1", {"start": v(-9.94, 71.75) * mm, "end": v(-15.2, 70.83) * mm});
            skLineSegment(sketch, "E17.35.2", {"start": v(-7.98, 60.62) * mm, "end": v(-9.94, 71.75) * mm});
            skLineSegment(sketch, "E17.35.3", {"start": v(-7.98, 60.62) * mm, "end": v(-13.23, 59.7) * mm});
            skPoint(sketch, "E17.center", {"position": v(0, 0) * mm});
            skLineSegment(sketch, "E17.anchor1", {"start": v(0, 0) * mm, "end": v(-2.67, 61.09) * mm, "construction": true});
            skLineSegment(sketch, "E17.anchor2", {"start": v(0, 0) * mm, "end": v(-13.23, 59.7) * mm, "construction": true});
            skSolve(sketch);
        }
        {
            var Q0;
            Q0=makeQuery(id+"F12.imprint","IMPRINT",FACE,{"disambiguationData":[TD([[makeQuery(id+"F12.imprint","IMPRINT",EDGE,{"derivedFrom":sQuery(id+"F12.wireOp",EDGE,"E17.1.0")}),-1.0]])]});
            var Q1;
            Q1=makeQuery(id+"F12.imprint","IMPRINT",FACE,{"disambiguationData":[TD([[makeQuery(id+"F12.imprint","IMPRINT",EDGE,{"derivedFrom":sQuery(id+"F12.wireOp",EDGE,"E16.bottom")}),-1.0]])]});
            var Q2;
            Q2=makeQuery(id+"F12.imprint","IMPRINT",FACE,{"disambiguationData":[TD([[makeQuery(id+"F12.imprint","IMPRINT",EDGE,{"derivedFrom":sQuery(id+"F12.wireOp",EDGE,"E17.2.0")}),-1.0]])]});
            var Q3;
            Q3=makeQuery(id+"F12.imprint","IMPRINT",FACE,{"disambiguationData":[TD([[makeQuery(id+"F12.imprint","IMPRINT",EDGE,{"derivedFrom":sQuery(id+"F12.wireOp",EDGE,"E17.3.0")}),-1.0]])]});
            var Q4;
            Q4=makeQuery(id+"F12.imprint","IMPRINT",FACE,{"disambiguationData":[TD([[makeQuery(id+"F12.imprint","IMPRINT",EDGE,{"derivedFrom":sQuery(id+"F12.wireOp",EDGE,"E17.4.0")}),-1.0]])]});
            var Q5;
            Q5=makeQuery(id+"F12.imprint","IMPRINT",FACE,{"disambiguationData":[TD([[makeQuery(id+"F12.imprint","IMPRINT",EDGE,{"derivedFrom":sQuery(id+"F12.wireOp",EDGE,"E17.5.0")}),-1.0]])]});
            var Q6;
            Q6=makeQuery(id+"F12.imprint","IMPRINT",FACE,{"disambiguationData":[TD([[makeQuery(id+"F12.imprint","IMPRINT",EDGE,{"derivedFrom":sQuery(id+"F12.wireOp",EDGE,"E17.6.0")}),-1.0]])]});
            var Q7;
            Q7=makeQuery(id+"F12.imprint","IMPRINT",FACE,{"disambiguationData":[TD([[makeQuery(id+"F12.imprint","IMPRINT",EDGE,{"derivedFrom":sQuery(id+"F12.wireOp",EDGE,"E17.7.0")}),-1.0]])]});
            var Q8;
            Q8=makeQuery(id+"F12.imprint","IMPRINT",FACE,{"disambiguationData":[TD([[makeQuery(id+"F12.imprint","IMPRINT",EDGE,{"derivedFrom":sQuery(id+"F12.wireOp",EDGE,"E17.8.0")}),-1.0]])]});
            var Q9;
            Q9=makeQuery(id+"F12.imprint","IMPRINT",FACE,{"disambiguationData":[TD([[makeQuery(id+"F12.imprint","IMPRINT",EDGE,{"derivedFrom":sQuery(id+"F12.wireOp",EDGE,"E17.9.0")}),-1.0]])]});
            var Q10;
            Q10=makeQuery(id+"F12.imprint","IMPRINT",FACE,{"disambiguationData":[TD([[makeQuery(id+"F12.imprint","IMPRINT",EDGE,{"derivedFrom":sQuery(id+"F12.wireOp",EDGE,"E17.10.0")}),-1.0]])]});
            var Q11;
            Q11=makeQuery(id+"F12.imprint","IMPRINT",FACE,{"disambiguationData":[TD([[makeQuery(id+"F12.imprint","IMPRINT",EDGE,{"derivedFrom":sQuery(id+"F12.wireOp",EDGE,"E17.11.0")}),-1.0]])]});
            var Q12;
            Q12=makeQuery(id+"F12.imprint","IMPRINT",FACE,{"disambiguationData":[TD([[makeQuery(id+"F12.imprint","IMPRINT",EDGE,{"derivedFrom":sQuery(id+"F12.wireOp",EDGE,"E17.12.0")}),-1.0]])]});
            var Q13;
            Q13=makeQuery(id+"F12.imprint","IMPRINT",FACE,{"disambiguationData":[TD([[makeQuery(id+"F12.imprint","IMPRINT",EDGE,{"derivedFrom":sQuery(id+"F12.wireOp",EDGE,"E17.13.0")}),-1.0]])]});
            var Q14;
            Q14=makeQuery(id+"F12.imprint","IMPRINT",FACE,{"disambiguationData":[TD([[makeQuery(id+"F12.imprint","IMPRINT",EDGE,{"derivedFrom":sQuery(id+"F12.wireOp",EDGE,"E17.14.0")}),-1.0]])]});
            var Q15;
            Q15=makeQuery(id+"F12.imprint","IMPRINT",FACE,{"disambiguationData":[TD([[makeQuery(id+"F12.imprint","IMPRINT",EDGE,{"derivedFrom":sQuery(id+"F12.wireOp",EDGE,"E17.15.0")}),-1.0]])]});
            var Q16;
            Q16=makeQuery(id+"F12.imprint","IMPRINT",FACE,{"disambiguationData":[TD([[makeQuery(id+"F12.imprint","IMPRINT",EDGE,{"derivedFrom":sQuery(id+"F12.wireOp",EDGE,"E17.16.0")}),-1.0]])]});
            var Q17;
            Q17=makeQuery(id+"F12.imprint","IMPRINT",FACE,{"disambiguationData":[TD([[makeQuery(id+"F12.imprint","IMPRINT",EDGE,{"derivedFrom":sQuery(id+"F12.wireOp",EDGE,"E17.17.0")}),-1.0]])]});
            var Q18;
            Q18=makeQuery(id+"F12.imprint","IMPRINT",FACE,{"disambiguationData":[TD([[makeQuery(id+"F12.imprint","IMPRINT",EDGE,{"derivedFrom":sQuery(id+"F12.wireOp",EDGE,"E17.18.0")}),-1.0]])]});
            var Q19;
            Q19=makeQuery(id+"F12.imprint","IMPRINT",FACE,{"disambiguationData":[TD([[makeQuery(id+"F12.imprint","IMPRINT",EDGE,{"derivedFrom":sQuery(id+"F12.wireOp",EDGE,"E17.19.0")}),-1.0]])]});
            var Q20;
            Q20=makeQuery(id+"F12.imprint","IMPRINT",FACE,{"disambiguationData":[TD([[makeQuery(id+"F12.imprint","IMPRINT",EDGE,{"derivedFrom":sQuery(id+"F12.wireOp",EDGE,"E17.20.0")}),-1.0]])]});
            var Q21;
            Q21=makeQuery(id+"F12.imprint","IMPRINT",FACE,{"disambiguationData":[TD([[makeQuery(id+"F12.imprint","IMPRINT",EDGE,{"derivedFrom":sQuery(id+"F12.wireOp",EDGE,"E17.21.0")}),-1.0]])]});
            var Q22;
            Q22=makeQuery(id+"F12.imprint","IMPRINT",FACE,{"disambiguationData":[TD([[makeQuery(id+"F12.imprint","IMPRINT",EDGE,{"derivedFrom":sQuery(id+"F12.wireOp",EDGE,"E17.22.0")}),-1.0]])]});
            var Q23;
            Q23=makeQuery(id+"F12.imprint","IMPRINT",FACE,{"disambiguationData":[TD([[makeQuery(id+"F12.imprint","IMPRINT",EDGE,{"derivedFrom":sQuery(id+"F12.wireOp",EDGE,"E17.23.0")}),-1.0]])]});
            var Q24;
            Q24=makeQuery(id+"F12.imprint","IMPRINT",FACE,{"disambiguationData":[TD([[makeQuery(id+"F12.imprint","IMPRINT",EDGE,{"derivedFrom":sQuery(id+"F12.wireOp",EDGE,"E17.24.0")}),-1.0]])]});
            var Q25;
            Q25=makeQuery(id+"F12.imprint","IMPRINT",FACE,{"disambiguationData":[TD([[makeQuery(id+"F12.imprint","IMPRINT",EDGE,{"derivedFrom":sQuery(id+"F12.wireOp",EDGE,"E17.25.0")}),-1.0]])]});
            var Q26;
            Q26=makeQuery(id+"F12.imprint","IMPRINT",FACE,{"disambiguationData":[TD([[makeQuery(id+"F12.imprint","IMPRINT",EDGE,{"derivedFrom":sQuery(id+"F12.wireOp",EDGE,"E17.26.0")}),-1.0]])]});
            var Q27;
            Q27=makeQuery(id+"F12.imprint","IMPRINT",FACE,{"disambiguationData":[TD([[makeQuery(id+"F12.imprint","IMPRINT",EDGE,{"derivedFrom":sQuery(id+"F12.wireOp",EDGE,"E17.27.0")}),-1.0]])]});
            var Q28;
            Q28=makeQuery(id+"F12.imprint","IMPRINT",FACE,{"disambiguationData":[TD([[makeQuery(id+"F12.imprint","IMPRINT",EDGE,{"derivedFrom":sQuery(id+"F12.wireOp",EDGE,"E17.28.0")}),-1.0]])]});
            var Q29;
            Q29=makeQuery(id+"F12.imprint","IMPRINT",FACE,{"disambiguationData":[TD([[makeQuery(id+"F12.imprint","IMPRINT",EDGE,{"derivedFrom":sQuery(id+"F12.wireOp",EDGE,"E17.29.0")}),-1.0]])]});
            var Q30;
            Q30=makeQuery(id+"F12.imprint","IMPRINT",FACE,{"disambiguationData":[TD([[makeQuery(id+"F12.imprint","IMPRINT",EDGE,{"derivedFrom":sQuery(id+"F12.wireOp",EDGE,"E17.30.0")}),-1.0]])]});
            var Q31;
            Q31=makeQuery(id+"F12.imprint","IMPRINT",FACE,{"disambiguationData":[TD([[makeQuery(id+"F12.imprint","IMPRINT",EDGE,{"derivedFrom":sQuery(id+"F12.wireOp",EDGE,"E17.31.0")}),-1.0]])]});
            var Q32;
            Q32=makeQuery(id+"F12.imprint","IMPRINT",FACE,{"disambiguationData":[TD([[makeQuery(id+"F12.imprint","IMPRINT",EDGE,{"derivedFrom":sQuery(id+"F12.wireOp",EDGE,"E17.32.0")}),-1.0]])]});
            var Q33;
            Q33=makeQuery(id+"F12.imprint","IMPRINT",FACE,{"disambiguationData":[TD([[makeQuery(id+"F12.imprint","IMPRINT",EDGE,{"derivedFrom":sQuery(id+"F12.wireOp",EDGE,"E17.33.0")}),-1.0]])]});
            var Q34;
            Q34=makeQuery(id+"F12.imprint","IMPRINT",FACE,{"disambiguationData":[TD([[makeQuery(id+"F12.imprint","IMPRINT",EDGE,{"derivedFrom":sQuery(id+"F12.wireOp",EDGE,"E17.34.0")}),-1.0]])]});
            var Q35;
            Q35=makeQuery(id+"F12.imprint","IMPRINT",FACE,{"disambiguationData":[TD([[makeQuery(id+"F12.imprint","IMPRINT",EDGE,{"derivedFrom":sQuery(id+"F12.wireOp",EDGE,"E17.35.0")}),-1.0]])]});
            extrude(context, id + "F13", {"entities" : qUnion([Q0, Q1, Q2, Q3, Q4, Q5, Q6, Q7, Q8, Q9, Q10, Q11, Q12, Q13, Q14, Q15, Q16, Q17, Q18, Q19, Q20, Q21, Q22, Q23, Q24, Q25, Q26, Q27, Q28, Q29, Q30, Q31, Q32, Q33, Q34, Q35]), "operationType" : NewBodyOperationType.ADD, "endBound" : BoundingType.SYMMETRIC, "depth" : 5.33 * mm});
        }
        {
            var Q0;
            Q0=makeQuery(id+"F13.opExtrude","CAP_EDGE",EDGE,{"disambiguationData":[OSD([sQuery(id+"F12.wireOp",EDGE,"E17.35.2")])],"isStart":false});
            var Q1;
            Q1=makeQuery(id+"F13.opExtrude","CAP_EDGE",EDGE,{"disambiguationData":[OSD([sQuery(id+"F12.wireOp",EDGE,"E17.35.0")])],"isStart":false});
            var Q2;
            Q2=makeQuery(id+"F13.opExtrude","CAP_EDGE",EDGE,{"disambiguationData":[OSD([sQuery(id+"F12.wireOp",EDGE,"E16.right")])],"isStart":false});
            var Q3;
            Q3=makeQuery(id+"F13.opExtrude","CAP_EDGE",EDGE,{"disambiguationData":[OSD([sQuery(id+"F12.wireOp",EDGE,"E16.left")])],"isStart":false});
            var Q4;
            Q4=makeQuery(id+"F13.opExtrude","CAP_EDGE",EDGE,{"disambiguationData":[OSD([sQuery(id+"F12.wireOp",EDGE,"E16.right")])],"isStart":true});
            var Q5;
            Q5=makeQuery(id+"F13.opExtrude","CAP_EDGE",EDGE,{"disambiguationData":[OSD([sQuery(id+"F12.wireOp",EDGE,"E17.35.0")])],"isStart":true});
            var Q6;
            Q6=makeQuery(id+"F13.opExtrude","CAP_EDGE",EDGE,{"disambiguationData":[OSD([sQuery(id+"F12.wireOp",EDGE,"E16.left")])],"isStart":true});
            var Q7;
            Q7=makeQuery(id+"F13.opExtrude","CAP_EDGE",EDGE,{"disambiguationData":[OSD([sQuery(id+"F12.wireOp",EDGE,"E17.35.2")])],"isStart":true});
            var Q8;
            Q8=makeQuery(id+"F13.opExtrude","CAP_EDGE",EDGE,{"disambiguationData":[OSD([sQuery(id+"F12.wireOp",EDGE,"E17.34.2")])],"isStart":false});
            var Q9;
            Q9=makeQuery(id+"F13.opExtrude","CAP_EDGE",EDGE,{"disambiguationData":[OSD([sQuery(id+"F12.wireOp",EDGE,"E17.34.2")])],"isStart":true});
            var Q10;
            Q10=makeQuery(id+"F13.opExtrude","CAP_EDGE",EDGE,{"disambiguationData":[OSD([sQuery(id+"F12.wireOp",EDGE,"E17.34.0")])],"isStart":false});
            var Q11;
            Q11=makeQuery(id+"F13.opExtrude","CAP_EDGE",EDGE,{"disambiguationData":[OSD([sQuery(id+"F12.wireOp",EDGE,"E17.33.2")])],"isStart":false});
            var Q12;
            Q12=makeQuery(id+"F13.opExtrude","CAP_EDGE",EDGE,{"disambiguationData":[OSD([sQuery(id+"F12.wireOp",EDGE,"E17.33.2")])],"isStart":true});
            var Q13;
            Q13=makeQuery(id+"F13.opExtrude","CAP_EDGE",EDGE,{"disambiguationData":[OSD([sQuery(id+"F12.wireOp",EDGE,"E17.33.0")])],"isStart":false});
            var Q14;
            Q14=makeQuery(id+"F13.opExtrude","CAP_EDGE",EDGE,{"disambiguationData":[OSD([sQuery(id+"F12.wireOp",EDGE,"E17.32.2")])],"isStart":false});
            var Q15;
            Q15=makeQuery(id+"F13.opExtrude","CAP_EDGE",EDGE,{"disambiguationData":[OSD([sQuery(id+"F12.wireOp",EDGE,"E17.32.2")])],"isStart":true});
            var Q16;
            Q16=makeQuery(id+"F13.opExtrude","CAP_EDGE",EDGE,{"disambiguationData":[OSD([sQuery(id+"F12.wireOp",EDGE,"E17.32.0")])],"isStart":false});
            var Q17;
            Q17=makeQuery(id+"F13.opExtrude","CAP_EDGE",EDGE,{"disambiguationData":[OSD([sQuery(id+"F12.wireOp",EDGE,"E17.31.2")])],"isStart":false});
            var Q18;
            Q18=makeQuery(id+"F13.opExtrude","CAP_EDGE",EDGE,{"disambiguationData":[OSD([sQuery(id+"F12.wireOp",EDGE,"E17.31.0")])],"isStart":false});
            var Q19;
            Q19=makeQuery(id+"F13.opExtrude","CAP_EDGE",EDGE,{"disambiguationData":[OSD([sQuery(id+"F12.wireOp",EDGE,"E17.30.2")])],"isStart":false});
            var Q20;
            Q20=makeQuery(id+"F13.opExtrude","CAP_EDGE",EDGE,{"disambiguationData":[OSD([sQuery(id+"F12.wireOp",EDGE,"E17.30.0")])],"isStart":false});
            var Q21;
            Q21=makeQuery(id+"F13.opExtrude","CAP_EDGE",EDGE,{"disambiguationData":[OSD([sQuery(id+"F12.wireOp",EDGE,"E17.29.2")])],"isStart":false});
            var Q22;
            Q22=makeQuery(id+"F13.opExtrude","CAP_EDGE",EDGE,{"disambiguationData":[OSD([sQuery(id+"F12.wireOp",EDGE,"E17.29.0")])],"isStart":false});
            var Q23;
            Q23=makeQuery(id+"F13.opExtrude","CAP_EDGE",EDGE,{"disambiguationData":[OSD([sQuery(id+"F12.wireOp",EDGE,"E17.31.0")])],"isStart":true});
            var Q24;
            Q24=makeQuery(id+"F13.opExtrude","CAP_EDGE",EDGE,{"disambiguationData":[OSD([sQuery(id+"F12.wireOp",EDGE,"E17.32.0")])],"isStart":true});
            var Q25;
            Q25=makeQuery(id+"F13.opExtrude","CAP_EDGE",EDGE,{"disambiguationData":[OSD([sQuery(id+"F12.wireOp",EDGE,"E17.33.0")])],"isStart":true});
            var Q26;
            Q26=makeQuery(id+"F13.opExtrude","CAP_EDGE",EDGE,{"disambiguationData":[OSD([sQuery(id+"F12.wireOp",EDGE,"E17.34.0")])],"isStart":true});
            var Q27;
            Q27=makeQuery(id+"F13.opExtrude","CAP_EDGE",EDGE,{"disambiguationData":[OSD([sQuery(id+"F12.wireOp",EDGE,"E17.30.0")])],"isStart":true});
            var Q28;
            Q28=makeQuery(id+"F13.opExtrude","CAP_EDGE",EDGE,{"disambiguationData":[OSD([sQuery(id+"F12.wireOp",EDGE,"E17.29.0")])],"isStart":true});
            var Q29;
            Q29=makeQuery(id+"F13.opExtrude","CAP_EDGE",EDGE,{"disambiguationData":[OSD([sQuery(id+"F12.wireOp",EDGE,"E17.31.2")])],"isStart":true});
            var Q30;
            Q30=makeQuery(id+"F13.opExtrude","CAP_EDGE",EDGE,{"disambiguationData":[OSD([sQuery(id+"F12.wireOp",EDGE,"E17.30.2")])],"isStart":true});
            var Q31;
            Q31=makeQuery(id+"F13.opExtrude","CAP_EDGE",EDGE,{"disambiguationData":[OSD([sQuery(id+"F12.wireOp",EDGE,"E17.29.2")])],"isStart":true});
            var Q32;
            Q32=makeQuery(id+"F13.opExtrude","CAP_EDGE",EDGE,{"disambiguationData":[OSD([sQuery(id+"F12.wireOp",EDGE,"E17.28.2")])],"isStart":false});
            var Q33;
            Q33=makeQuery(id+"F13.opExtrude","CAP_EDGE",EDGE,{"disambiguationData":[OSD([sQuery(id+"F12.wireOp",EDGE,"E17.28.0")])],"isStart":false});
            var Q34;
            Q34=makeQuery(id+"F13.opExtrude","CAP_EDGE",EDGE,{"disambiguationData":[OSD([sQuery(id+"F12.wireOp",EDGE,"E17.28.2")])],"isStart":true});
            var Q35;
            Q35=makeQuery(id+"F13.opExtrude","CAP_EDGE",EDGE,{"disambiguationData":[OSD([sQuery(id+"F12.wireOp",EDGE,"E17.27.2")])],"isStart":false});
            var Q36;
            Q36=makeQuery(id+"F13.opExtrude","CAP_EDGE",EDGE,{"disambiguationData":[OSD([sQuery(id+"F12.wireOp",EDGE,"E17.27.0")])],"isStart":false});
            var Q37;
            Q37=makeQuery(id+"F13.opExtrude","CAP_EDGE",EDGE,{"disambiguationData":[OSD([sQuery(id+"F12.wireOp",EDGE,"E17.28.0")])],"isStart":true});
            var Q38;
            Q38=makeQuery(id+"F13.opExtrude","CAP_EDGE",EDGE,{"disambiguationData":[OSD([sQuery(id+"F12.wireOp",EDGE,"E17.27.0")])],"isStart":true});
            var Q39;
            Q39=makeQuery(id+"F13.opExtrude","CAP_EDGE",EDGE,{"disambiguationData":[OSD([sQuery(id+"F12.wireOp",EDGE,"E17.26.0")])],"isStart":true});
            var Q40;
            Q40=makeQuery(id+"F13.opExtrude","CAP_EDGE",EDGE,{"disambiguationData":[OSD([sQuery(id+"F12.wireOp",EDGE,"E17.26.0")])],"isStart":false});
            var Q41;
            Q41=makeQuery(id+"F13.opExtrude","CAP_EDGE",EDGE,{"disambiguationData":[OSD([sQuery(id+"F12.wireOp",EDGE,"E17.26.2")])],"isStart":false});
            var Q42;
            Q42=makeQuery(id+"F13.opExtrude","CAP_EDGE",EDGE,{"disambiguationData":[OSD([sQuery(id+"F12.wireOp",EDGE,"E17.25.2")])],"isStart":false});
            var Q43;
            Q43=makeQuery(id+"F13.opExtrude","CAP_EDGE",EDGE,{"disambiguationData":[OSD([sQuery(id+"F12.wireOp",EDGE,"E17.25.0")])],"isStart":false});
            var Q44;
            Q44=makeQuery(id+"F13.opExtrude","CAP_EDGE",EDGE,{"disambiguationData":[OSD([sQuery(id+"F12.wireOp",EDGE,"E17.25.0")])],"isStart":true});
            var Q45;
            Q45=makeQuery(id+"F13.opExtrude","CAP_EDGE",EDGE,{"disambiguationData":[OSD([sQuery(id+"F12.wireOp",EDGE,"E17.24.2")])],"isStart":false});
            var Q46;
            Q46=makeQuery(id+"F13.opExtrude","CAP_EDGE",EDGE,{"disambiguationData":[OSD([sQuery(id+"F12.wireOp",EDGE,"E17.24.0")])],"isStart":false});
            var Q47;
            Q47=makeQuery(id+"F13.opExtrude","CAP_EDGE",EDGE,{"disambiguationData":[OSD([sQuery(id+"F12.wireOp",EDGE,"E17.27.2")])],"isStart":true});
            var Q48;
            Q48=makeQuery(id+"F13.opExtrude","CAP_EDGE",EDGE,{"disambiguationData":[OSD([sQuery(id+"F12.wireOp",EDGE,"E17.26.2")])],"isStart":true});
            var Q49;
            Q49=makeQuery(id+"F13.opExtrude","CAP_EDGE",EDGE,{"disambiguationData":[OSD([sQuery(id+"F12.wireOp",EDGE,"E17.25.2")])],"isStart":true});
            var Q50;
            Q50=makeQuery(id+"F13.opExtrude","CAP_EDGE",EDGE,{"disambiguationData":[OSD([sQuery(id+"F12.wireOp",EDGE,"E17.24.0")])],"isStart":true});
            var Q51;
            Q51=makeQuery(id+"F13.opExtrude","CAP_EDGE",EDGE,{"disambiguationData":[OSD([sQuery(id+"F12.wireOp",EDGE,"E17.24.2")])],"isStart":true});
            var Q52;
            Q52=makeQuery(id+"F13.opExtrude","CAP_EDGE",EDGE,{"disambiguationData":[OSD([sQuery(id+"F12.wireOp",EDGE,"E17.23.2")])],"isStart":true});
            var Q53;
            Q53=makeQuery(id+"F13.opExtrude","CAP_EDGE",EDGE,{"disambiguationData":[OSD([sQuery(id+"F12.wireOp",EDGE,"E17.23.0")])],"isStart":true});
            var Q54;
            Q54=makeQuery(id+"F13.opExtrude","CAP_EDGE",EDGE,{"disambiguationData":[OSD([sQuery(id+"F12.wireOp",EDGE,"E17.22.2")])],"isStart":true});
            var Q55;
            Q55=makeQuery(id+"F13.opExtrude","CAP_EDGE",EDGE,{"disambiguationData":[OSD([sQuery(id+"F12.wireOp",EDGE,"E17.22.0")])],"isStart":true});
            var Q56;
            Q56=makeQuery(id+"F13.opExtrude","CAP_EDGE",EDGE,{"disambiguationData":[OSD([sQuery(id+"F12.wireOp",EDGE,"E17.21.2")])],"isStart":true});
            var Q57;
            Q57=makeQuery(id+"F13.opExtrude","CAP_EDGE",EDGE,{"disambiguationData":[OSD([sQuery(id+"F12.wireOp",EDGE,"E17.21.0")])],"isStart":true});
            var Q58;
            Q58=makeQuery(id+"F13.opExtrude","CAP_EDGE",EDGE,{"disambiguationData":[OSD([sQuery(id+"F12.wireOp",EDGE,"E17.20.2")])],"isStart":true});
            var Q59;
            Q59=makeQuery(id+"F13.opExtrude","CAP_EDGE",EDGE,{"disambiguationData":[OSD([sQuery(id+"F12.wireOp",EDGE,"E17.20.0")])],"isStart":true});
            var Q60;
            Q60=makeQuery(id+"F13.opExtrude","CAP_EDGE",EDGE,{"disambiguationData":[OSD([sQuery(id+"F12.wireOp",EDGE,"E17.21.2")])],"isStart":false});
            var Q61;
            Q61=makeQuery(id+"F13.opExtrude","CAP_EDGE",EDGE,{"disambiguationData":[OSD([sQuery(id+"F12.wireOp",EDGE,"E17.22.2")])],"isStart":false});
            var Q62;
            Q62=makeQuery(id+"F13.opExtrude","CAP_EDGE",EDGE,{"disambiguationData":[OSD([sQuery(id+"F12.wireOp",EDGE,"E17.20.2")])],"isStart":false});
            var Q63;
            Q63=makeQuery(id+"F13.opExtrude","CAP_EDGE",EDGE,{"disambiguationData":[OSD([sQuery(id+"F12.wireOp",EDGE,"E17.23.2")])],"isStart":false});
            var Q64;
            Q64=makeQuery(id+"F13.opExtrude","CAP_EDGE",EDGE,{"disambiguationData":[OSD([sQuery(id+"F12.wireOp",EDGE,"E17.23.0")])],"isStart":false});
            var Q65;
            Q65=makeQuery(id+"F13.opExtrude","CAP_EDGE",EDGE,{"disambiguationData":[OSD([sQuery(id+"F12.wireOp",EDGE,"E17.22.0")])],"isStart":false});
            var Q66;
            Q66=makeQuery(id+"F13.opExtrude","CAP_EDGE",EDGE,{"disambiguationData":[OSD([sQuery(id+"F12.wireOp",EDGE,"E17.21.0")])],"isStart":false});
            var Q67;
            Q67=makeQuery(id+"F13.opExtrude","CAP_EDGE",EDGE,{"disambiguationData":[OSD([sQuery(id+"F12.wireOp",EDGE,"E17.20.0")])],"isStart":false});
            var Q68;
            Q68=makeQuery(id+"F13.opExtrude","CAP_EDGE",EDGE,{"disambiguationData":[OSD([sQuery(id+"F12.wireOp",EDGE,"E17.19.2")])],"isStart":false});
            var Q69;
            Q69=makeQuery(id+"F13.opExtrude","CAP_EDGE",EDGE,{"disambiguationData":[OSD([sQuery(id+"F12.wireOp",EDGE,"E17.19.2")])],"isStart":true});
            var Q70;
            Q70=makeQuery(id+"F13.opExtrude","CAP_EDGE",EDGE,{"disambiguationData":[OSD([sQuery(id+"F12.wireOp",EDGE,"E17.19.0")])],"isStart":false});
            var Q71;
            Q71=makeQuery(id+"F13.opExtrude","CAP_EDGE",EDGE,{"disambiguationData":[OSD([sQuery(id+"F12.wireOp",EDGE,"E17.19.0")])],"isStart":true});
            var Q72;
            Q72=makeQuery(id+"F13.opExtrude","CAP_EDGE",EDGE,{"disambiguationData":[OSD([sQuery(id+"F12.wireOp",EDGE,"E17.18.0")])],"isStart":true});
            var Q73;
            Q73=makeQuery(id+"F13.opExtrude","CAP_EDGE",EDGE,{"disambiguationData":[OSD([sQuery(id+"F12.wireOp",EDGE,"E17.18.2")])],"isStart":true});
            var Q74;
            Q74=makeQuery(id+"F13.opExtrude","CAP_EDGE",EDGE,{"disambiguationData":[OSD([sQuery(id+"F12.wireOp",EDGE,"E17.18.0")])],"isStart":false});
            var Q75;
            Q75=makeQuery(id+"F13.opExtrude","CAP_EDGE",EDGE,{"disambiguationData":[OSD([sQuery(id+"F12.wireOp",EDGE,"E17.17.0")])],"isStart":true});
            var Q76;
            Q76=makeQuery(id+"F13.opExtrude","CAP_EDGE",EDGE,{"disambiguationData":[OSD([sQuery(id+"F12.wireOp",EDGE,"E17.17.2")])],"isStart":true});
            var Q77;
            Q77=makeQuery(id+"F13.opExtrude","CAP_EDGE",EDGE,{"disambiguationData":[OSD([sQuery(id+"F12.wireOp",EDGE,"E17.17.0")])],"isStart":false});
            var Q78;
            Q78=makeQuery(id+"F13.opExtrude","CAP_EDGE",EDGE,{"disambiguationData":[OSD([sQuery(id+"F12.wireOp",EDGE,"E17.16.0")])],"isStart":true});
            var Q79;
            Q79=makeQuery(id+"F13.opExtrude","CAP_EDGE",EDGE,{"disambiguationData":[OSD([sQuery(id+"F12.wireOp",EDGE,"E17.16.2")])],"isStart":true});
            var Q80;
            Q80=makeQuery(id+"F13.opExtrude","CAP_EDGE",EDGE,{"disambiguationData":[OSD([sQuery(id+"F12.wireOp",EDGE,"E17.16.0")])],"isStart":false});
            var Q81;
            Q81=makeQuery(id+"F13.opExtrude","CAP_EDGE",EDGE,{"disambiguationData":[OSD([sQuery(id+"F12.wireOp",EDGE,"E17.15.2")])],"isStart":true});
            var Q82;
            Q82=makeQuery(id+"F13.opExtrude","CAP_EDGE",EDGE,{"disambiguationData":[OSD([sQuery(id+"F12.wireOp",EDGE,"E17.15.0")])],"isStart":true});
            var Q83;
            Q83=makeQuery(id+"F13.opExtrude","CAP_EDGE",EDGE,{"disambiguationData":[OSD([sQuery(id+"F12.wireOp",EDGE,"E17.15.0")])],"isStart":false});
            var Q84;
            Q84=makeQuery(id+"F13.opExtrude","CAP_EDGE",EDGE,{"disambiguationData":[OSD([sQuery(id+"F12.wireOp",EDGE,"E17.14.2")])],"isStart":true});
            var Q85;
            Q85=makeQuery(id+"F13.opExtrude","CAP_EDGE",EDGE,{"disambiguationData":[OSD([sQuery(id+"F12.wireOp",EDGE,"E17.18.2")])],"isStart":false});
            var Q86;
            Q86=makeQuery(id+"F13.opExtrude","CAP_EDGE",EDGE,{"disambiguationData":[OSD([sQuery(id+"F12.wireOp",EDGE,"E17.17.2")])],"isStart":false});
            var Q87;
            Q87=makeQuery(id+"F13.opExtrude","CAP_EDGE",EDGE,{"disambiguationData":[OSD([sQuery(id+"F12.wireOp",EDGE,"E17.16.2")])],"isStart":false});
            var Q88;
            Q88=makeQuery(id+"F13.opExtrude","CAP_EDGE",EDGE,{"disambiguationData":[OSD([sQuery(id+"F12.wireOp",EDGE,"E17.15.2")])],"isStart":false});
            var Q89;
            Q89=makeQuery(id+"F13.opExtrude","CAP_EDGE",EDGE,{"disambiguationData":[OSD([sQuery(id+"F12.wireOp",EDGE,"E17.14.0")])],"isStart":false});
            var Q90;
            Q90=makeQuery(id+"F13.opExtrude","CAP_EDGE",EDGE,{"disambiguationData":[OSD([sQuery(id+"F12.wireOp",EDGE,"E17.14.2")])],"isStart":false});
            var Q91;
            Q91=makeQuery(id+"F13.opExtrude","CAP_EDGE",EDGE,{"disambiguationData":[OSD([sQuery(id+"F12.wireOp",EDGE,"E17.14.0")])],"isStart":true});
            var Q92;
            Q92=makeQuery(id+"F13.opExtrude","CAP_EDGE",EDGE,{"disambiguationData":[OSD([sQuery(id+"F12.wireOp",EDGE,"E17.13.2")])],"isStart":false});
            var Q93;
            Q93=makeQuery(id+"F13.opExtrude","CAP_EDGE",EDGE,{"disambiguationData":[OSD([sQuery(id+"F12.wireOp",EDGE,"E17.13.2")])],"isStart":true});
            var Q94;
            Q94=makeQuery(id+"F13.opExtrude","CAP_EDGE",EDGE,{"disambiguationData":[OSD([sQuery(id+"F12.wireOp",EDGE,"E17.12.2")])],"isStart":false});
            var Q95;
            Q95=makeQuery(id+"F13.opExtrude","CAP_EDGE",EDGE,{"disambiguationData":[OSD([sQuery(id+"F12.wireOp",EDGE,"E17.13.0")])],"isStart":false});
            var Q96;
            Q96=makeQuery(id+"F13.opExtrude","CAP_EDGE",EDGE,{"disambiguationData":[OSD([sQuery(id+"F12.wireOp",EDGE,"E17.12.2")])],"isStart":true});
            var Q97;
            Q97=makeQuery(id+"F13.opExtrude","CAP_EDGE",EDGE,{"disambiguationData":[OSD([sQuery(id+"F12.wireOp",EDGE,"E17.12.0")])],"isStart":false});
            var Q98;
            Q98=makeQuery(id+"F13.opExtrude","CAP_EDGE",EDGE,{"disambiguationData":[OSD([sQuery(id+"F12.wireOp",EDGE,"E17.11.2")])],"isStart":true});
            var Q99;
            Q99=makeQuery(id+"F13.opExtrude","CAP_EDGE",EDGE,{"disambiguationData":[OSD([sQuery(id+"F12.wireOp",EDGE,"E17.11.2")])],"isStart":false});
            var Q100;
            Q100=makeQuery(id+"F13.opExtrude","CAP_EDGE",EDGE,{"disambiguationData":[OSD([sQuery(id+"F12.wireOp",EDGE,"E17.10.2")])],"isStart":false});
            var Q101;
            Q101=makeQuery(id+"F13.opExtrude","CAP_EDGE",EDGE,{"disambiguationData":[OSD([sQuery(id+"F12.wireOp",EDGE,"E17.10.0")])],"isStart":false});
            var Q102;
            Q102=makeQuery(id+"F13.opExtrude","CAP_EDGE",EDGE,{"disambiguationData":[OSD([sQuery(id+"F12.wireOp",EDGE,"E17.10.2")])],"isStart":true});
            var Q103;
            Q103=makeQuery(id+"F13.opExtrude","CAP_EDGE",EDGE,{"disambiguationData":[OSD([sQuery(id+"F12.wireOp",EDGE,"E17.13.0")])],"isStart":true});
            var Q104;
            Q104=makeQuery(id+"F13.opExtrude","CAP_EDGE",EDGE,{"disambiguationData":[OSD([sQuery(id+"F12.wireOp",EDGE,"E17.12.0")])],"isStart":true});
            var Q105;
            Q105=makeQuery(id+"F13.opExtrude","CAP_EDGE",EDGE,{"disambiguationData":[OSD([sQuery(id+"F12.wireOp",EDGE,"E17.11.0")])],"isStart":false});
            var Q106;
            Q106=makeQuery(id+"F13.opExtrude","CAP_EDGE",EDGE,{"disambiguationData":[OSD([sQuery(id+"F12.wireOp",EDGE,"E17.11.0")])],"isStart":true});
            var Q107;
            Q107=makeQuery(id+"F13.opExtrude","CAP_EDGE",EDGE,{"disambiguationData":[OSD([sQuery(id+"F12.wireOp",EDGE,"E17.10.0")])],"isStart":true});
            var Q108;
            Q108=makeQuery(id+"F13.opExtrude","CAP_EDGE",EDGE,{"disambiguationData":[OSD([sQuery(id+"F12.wireOp",EDGE,"E17.9.0")])],"isStart":true});
            var Q109;
            Q109=makeQuery(id+"F13.opExtrude","CAP_EDGE",EDGE,{"disambiguationData":[OSD([sQuery(id+"F12.wireOp",EDGE,"E17.9.2")])],"isStart":true});
            var Q110;
            Q110=makeQuery(id+"F13.opExtrude","CAP_EDGE",EDGE,{"disambiguationData":[OSD([sQuery(id+"F12.wireOp",EDGE,"E17.9.0")])],"isStart":false});
            var Q111;
            Q111=makeQuery(id+"F13.opExtrude","CAP_EDGE",EDGE,{"disambiguationData":[OSD([sQuery(id+"F12.wireOp",EDGE,"E17.8.0")])],"isStart":true});
            var Q112;
            Q112=makeQuery(id+"F13.opExtrude","CAP_EDGE",EDGE,{"disambiguationData":[OSD([sQuery(id+"F12.wireOp",EDGE,"E17.8.0")])],"isStart":false});
            var Q113;
            Q113=makeQuery(id+"F13.opExtrude","CAP_EDGE",EDGE,{"disambiguationData":[OSD([sQuery(id+"F12.wireOp",EDGE,"E17.8.2")])],"isStart":true});
            var Q114;
            Q114=makeQuery(id+"F13.opExtrude","CAP_EDGE",EDGE,{"disambiguationData":[OSD([sQuery(id+"F12.wireOp",EDGE,"E17.9.2")])],"isStart":false});
            var Q115;
            Q115=makeQuery(id+"F13.opExtrude","CAP_EDGE",EDGE,{"disambiguationData":[OSD([sQuery(id+"F12.wireOp",EDGE,"E17.8.2")])],"isStart":false});
            var Q116;
            Q116=makeQuery(id+"F13.opExtrude","CAP_EDGE",EDGE,{"disambiguationData":[OSD([sQuery(id+"F12.wireOp",EDGE,"E17.7.0")])],"isStart":true});
            var Q117;
            Q117=makeQuery(id+"F13.opExtrude","CAP_EDGE",EDGE,{"disambiguationData":[OSD([sQuery(id+"F12.wireOp",EDGE,"E17.7.2")])],"isStart":true});
            var Q118;
            Q118=makeQuery(id+"F13.opExtrude","CAP_EDGE",EDGE,{"disambiguationData":[OSD([sQuery(id+"F12.wireOp",EDGE,"E17.7.0")])],"isStart":false});
            var Q119;
            Q119=makeQuery(id+"F13.opExtrude","CAP_EDGE",EDGE,{"disambiguationData":[OSD([sQuery(id+"F12.wireOp",EDGE,"E17.6.0")])],"isStart":true});
            var Q120;
            Q120=makeQuery(id+"F13.opExtrude","CAP_EDGE",EDGE,{"disambiguationData":[OSD([sQuery(id+"F12.wireOp",EDGE,"E17.6.2")])],"isStart":true});
            var Q121;
            Q121=makeQuery(id+"F13.opExtrude","CAP_EDGE",EDGE,{"disambiguationData":[OSD([sQuery(id+"F12.wireOp",EDGE,"E17.6.0")])],"isStart":false});
            var Q122;
            Q122=makeQuery(id+"F13.opExtrude","CAP_EDGE",EDGE,{"disambiguationData":[OSD([sQuery(id+"F12.wireOp",EDGE,"E17.5.2")])],"isStart":true});
            var Q123;
            Q123=makeQuery(id+"F13.opExtrude","CAP_EDGE",EDGE,{"disambiguationData":[OSD([sQuery(id+"F12.wireOp",EDGE,"E17.5.0")])],"isStart":true});
            var Q124;
            Q124=makeQuery(id+"F13.opExtrude","CAP_EDGE",EDGE,{"disambiguationData":[OSD([sQuery(id+"F12.wireOp",EDGE,"E17.5.0")])],"isStart":false});
            var Q125;
            Q125=makeQuery(id+"F13.opExtrude","CAP_EDGE",EDGE,{"disambiguationData":[OSD([sQuery(id+"F12.wireOp",EDGE,"E17.4.2")])],"isStart":true});
            var Q126;
            Q126=makeQuery(id+"F13.opExtrude","CAP_EDGE",EDGE,{"disambiguationData":[OSD([sQuery(id+"F12.wireOp",EDGE,"E17.4.0")])],"isStart":true});
            var Q127;
            Q127=makeQuery(id+"F13.opExtrude","CAP_EDGE",EDGE,{"disambiguationData":[OSD([sQuery(id+"F12.wireOp",EDGE,"E17.4.0")])],"isStart":false});
            var Q128;
            Q128=makeQuery(id+"F13.opExtrude","CAP_EDGE",EDGE,{"disambiguationData":[OSD([sQuery(id+"F12.wireOp",EDGE,"E17.3.2")])],"isStart":true});
            var Q129;
            Q129=makeQuery(id+"F13.opExtrude","CAP_EDGE",EDGE,{"disambiguationData":[OSD([sQuery(id+"F12.wireOp",EDGE,"E17.3.0")])],"isStart":true});
            var Q130;
            Q130=makeQuery(id+"F13.opExtrude","CAP_EDGE",EDGE,{"disambiguationData":[OSD([sQuery(id+"F12.wireOp",EDGE,"E17.7.2")])],"isStart":false});
            var Q131;
            Q131=makeQuery(id+"F13.opExtrude","CAP_EDGE",EDGE,{"disambiguationData":[OSD([sQuery(id+"F12.wireOp",EDGE,"E17.6.2")])],"isStart":false});
            var Q132;
            Q132=makeQuery(id+"F13.opExtrude","CAP_EDGE",EDGE,{"disambiguationData":[OSD([sQuery(id+"F12.wireOp",EDGE,"E17.5.2")])],"isStart":false});
            var Q133;
            Q133=makeQuery(id+"F13.opExtrude","CAP_EDGE",EDGE,{"disambiguationData":[OSD([sQuery(id+"F12.wireOp",EDGE,"E17.4.2")])],"isStart":false});
            var Q134;
            Q134=makeQuery(id+"F13.opExtrude","CAP_EDGE",EDGE,{"disambiguationData":[OSD([sQuery(id+"F12.wireOp",EDGE,"E17.3.2")])],"isStart":false});
            var Q135;
            Q135=makeQuery(id+"F13.opExtrude","CAP_EDGE",EDGE,{"disambiguationData":[OSD([sQuery(id+"F12.wireOp",EDGE,"E17.3.0")])],"isStart":false});
            var Q136;
            Q136=makeQuery(id+"F13.opExtrude","CAP_EDGE",EDGE,{"disambiguationData":[OSD([sQuery(id+"F12.wireOp",EDGE,"E17.2.2")])],"isStart":false});
            var Q137;
            Q137=makeQuery(id+"F13.opExtrude","CAP_EDGE",EDGE,{"disambiguationData":[OSD([sQuery(id+"F12.wireOp",EDGE,"E17.2.2")])],"isStart":true});
            var Q138;
            Q138=makeQuery(id+"F13.opExtrude","CAP_EDGE",EDGE,{"disambiguationData":[OSD([sQuery(id+"F12.wireOp",EDGE,"E17.2.0")])],"isStart":false});
            var Q139;
            Q139=makeQuery(id+"F13.opExtrude","CAP_EDGE",EDGE,{"disambiguationData":[OSD([sQuery(id+"F12.wireOp",EDGE,"E17.1.2")])],"isStart":true});
            var Q140;
            Q140=makeQuery(id+"F13.opExtrude","CAP_EDGE",EDGE,{"disambiguationData":[OSD([sQuery(id+"F12.wireOp",EDGE,"E17.1.2")])],"isStart":false});
            var Q141;
            Q141=makeQuery(id+"F13.opExtrude","CAP_EDGE",EDGE,{"disambiguationData":[OSD([sQuery(id+"F12.wireOp",EDGE,"E17.1.0")])],"isStart":false});
            var Q142;
            Q142=makeQuery(id+"F13.opExtrude","CAP_EDGE",EDGE,{"disambiguationData":[OSD([sQuery(id+"F12.wireOp",EDGE,"E17.2.0")])],"isStart":true});
            var Q143;
            Q143=makeQuery(id+"F13.opExtrude","CAP_EDGE",EDGE,{"disambiguationData":[OSD([sQuery(id+"F12.wireOp",EDGE,"E17.1.0")])],"isStart":true});
            fillet(context, id + "F14", {"entities" : qUnion([Q0, Q1, Q2, Q3, Q4, Q5, Q6, Q7, Q8, Q9, Q10, Q11, Q12, Q13, Q14, Q15, Q16, Q17, Q18, Q19, Q20, Q21, Q22, Q23, Q24, Q25, Q26, Q27, Q28, Q29, Q30, Q31, Q32, Q33, Q34, Q35, Q36, Q37, Q38, Q39, Q40, Q41, Q42, Q43, Q44, Q45, Q46, Q47, Q48, Q49, Q50, Q51, Q52, Q53, Q54, Q55, Q56, Q57, Q58, Q59, Q60, Q61, Q62, Q63, Q64, Q65, Q66, Q67, Q68, Q69, Q70, Q71, Q72, Q73, Q74, Q75, Q76, Q77, Q78, Q79, Q80, Q81, Q82, Q83, Q84, Q85, Q86, Q87, Q88, Q89, Q90, Q91, Q92, Q93, Q94, Q95, Q96, Q97, Q98, Q99, Q100, Q101, Q102, Q103, Q104, Q105, Q106, Q107, Q108, Q109, Q110, Q111, Q112, Q113, Q114, Q115, Q116, Q117, Q118, Q119, Q120, Q121, Q122, Q123, Q124, Q125, Q126, Q127, Q128, Q129, Q130, Q131, Q132, Q133, Q134, Q135, Q136, Q137, Q138, Q139, Q140, Q141, Q142, Q143]), "radius" : 2.67 * mm, "tangentPropagation" : true, "allowEdgeOverflow" : false});
        }
        {
            var Q0;
            Q0=makeQuery(id+"F14.opFillet","BLEND_EDGE",EDGE,{"blendedFrom":[makeQuery(id+"F13.opExtrude","CAP_EDGE",EDGE,{"disambiguationData":[OSD([sQuery(id+"F12.wireOp",EDGE,"E16.left")])],"isStart":false}),makeQuery(id+"F13.opExtrude","SWEPT_FACE",FACE,{"disambiguationData":[OSD([sQuery(id+"F12.wireOp",EDGE,"E16.top")])]})],"blendedInto":[makeQuery(id+"F13.opExtrude","SWEPT_FACE",FACE,{"disambiguationData":[OSD([sQuery(id+"F12.wireOp",EDGE,"E16.top")])]})]});
            var Q1;
            Q1=makeQuery(id+"F14.opFillet","BLEND_EDGE",EDGE,{"blendedFrom":[makeQuery(id+"F13.opExtrude","CAP_EDGE",EDGE,{"disambiguationData":[OSD([sQuery(id+"F12.wireOp",EDGE,"E17.35.2")])],"isStart":false}),makeQuery(id+"F13.opExtrude","SWEPT_FACE",FACE,{"disambiguationData":[OSD([sQuery(id+"F12.wireOp",EDGE,"E17.35.1")])]})],"blendedInto":[makeQuery(id+"F13.opExtrude","SWEPT_FACE",FACE,{"disambiguationData":[OSD([sQuery(id+"F12.wireOp",EDGE,"E17.35.1")])]})]});
            var Q2;
            Q2=makeQuery(id+"F14.opFillet","BLEND_EDGE",EDGE,{"blendedFrom":[makeQuery(id+"F13.opExtrude","CAP_EDGE",EDGE,{"disambiguationData":[OSD([sQuery(id+"F12.wireOp",EDGE,"E17.34.2")])],"isStart":false}),makeQuery(id+"F13.opExtrude","SWEPT_FACE",FACE,{"disambiguationData":[OSD([sQuery(id+"F12.wireOp",EDGE,"E17.34.1")])]})],"blendedInto":[makeQuery(id+"F13.opExtrude","SWEPT_FACE",FACE,{"disambiguationData":[OSD([sQuery(id+"F12.wireOp",EDGE,"E17.34.1")])]})]});
            var Q3;
            Q3=makeQuery(id+"F14.opFillet","BLEND_EDGE",EDGE,{"blendedFrom":[makeQuery(id+"F13.opExtrude","CAP_EDGE",EDGE,{"disambiguationData":[OSD([sQuery(id+"F12.wireOp",EDGE,"E17.33.2")])],"isStart":false}),makeQuery(id+"F13.opExtrude","SWEPT_FACE",FACE,{"disambiguationData":[OSD([sQuery(id+"F12.wireOp",EDGE,"E17.33.1")])]})],"blendedInto":[makeQuery(id+"F13.opExtrude","SWEPT_FACE",FACE,{"disambiguationData":[OSD([sQuery(id+"F12.wireOp",EDGE,"E17.33.1")])]})]});
            var Q4;
            Q4=makeQuery(id+"F14.opFillet","BLEND_EDGE",EDGE,{"blendedFrom":[makeQuery(id+"F13.opExtrude","CAP_EDGE",EDGE,{"disambiguationData":[OSD([sQuery(id+"F12.wireOp",EDGE,"E17.32.2")])],"isStart":false}),makeQuery(id+"F13.opExtrude","SWEPT_FACE",FACE,{"disambiguationData":[OSD([sQuery(id+"F12.wireOp",EDGE,"E17.32.1")])]})],"blendedInto":[makeQuery(id+"F13.opExtrude","SWEPT_FACE",FACE,{"disambiguationData":[OSD([sQuery(id+"F12.wireOp",EDGE,"E17.32.1")])]})]});
            var Q5;
            Q5=makeQuery(id+"F14.opFillet","BLEND_EDGE",EDGE,{"blendedFrom":[makeQuery(id+"F13.opExtrude","CAP_EDGE",EDGE,{"disambiguationData":[OSD([sQuery(id+"F12.wireOp",EDGE,"E17.31.2")])],"isStart":false}),makeQuery(id+"F13.opExtrude","SWEPT_FACE",FACE,{"disambiguationData":[OSD([sQuery(id+"F12.wireOp",EDGE,"E17.31.1")])]})],"blendedInto":[makeQuery(id+"F13.opExtrude","SWEPT_FACE",FACE,{"disambiguationData":[OSD([sQuery(id+"F12.wireOp",EDGE,"E17.31.1")])]})]});
            var Q6;
            Q6=makeQuery(id+"F14.opFillet","BLEND_EDGE",EDGE,{"blendedFrom":[makeQuery(id+"F13.opExtrude","CAP_EDGE",EDGE,{"disambiguationData":[OSD([sQuery(id+"F12.wireOp",EDGE,"E17.30.2")])],"isStart":false}),makeQuery(id+"F13.opExtrude","SWEPT_FACE",FACE,{"disambiguationData":[OSD([sQuery(id+"F12.wireOp",EDGE,"E17.30.1")])]})],"blendedInto":[makeQuery(id+"F13.opExtrude","SWEPT_FACE",FACE,{"disambiguationData":[OSD([sQuery(id+"F12.wireOp",EDGE,"E17.30.1")])]})]});
            var Q7;
            Q7=makeQuery(id+"F14.opFillet","BLEND_EDGE",EDGE,{"blendedFrom":[makeQuery(id+"F13.opExtrude","CAP_EDGE",EDGE,{"disambiguationData":[OSD([sQuery(id+"F12.wireOp",EDGE,"E17.1.2")])],"isStart":false}),makeQuery(id+"F13.opExtrude","SWEPT_FACE",FACE,{"disambiguationData":[OSD([sQuery(id+"F12.wireOp",EDGE,"E17.1.1")])]})],"blendedInto":[makeQuery(id+"F13.opExtrude","SWEPT_FACE",FACE,{"disambiguationData":[OSD([sQuery(id+"F12.wireOp",EDGE,"E17.1.1")])]})]});
            var Q8;
            Q8=makeQuery(id+"F14.opFillet","BLEND_EDGE",EDGE,{"blendedFrom":[makeQuery(id+"F13.opExtrude","CAP_EDGE",EDGE,{"disambiguationData":[OSD([sQuery(id+"F12.wireOp",EDGE,"E17.2.2")])],"isStart":false}),makeQuery(id+"F13.opExtrude","SWEPT_FACE",FACE,{"disambiguationData":[OSD([sQuery(id+"F12.wireOp",EDGE,"E17.2.1")])]})],"blendedInto":[makeQuery(id+"F13.opExtrude","SWEPT_FACE",FACE,{"disambiguationData":[OSD([sQuery(id+"F12.wireOp",EDGE,"E17.2.1")])]})]});
            var Q9;
            Q9=makeQuery(id+"F14.opFillet","BLEND_EDGE",EDGE,{"blendedFrom":[makeQuery(id+"F13.opExtrude","CAP_EDGE",EDGE,{"disambiguationData":[OSD([sQuery(id+"F12.wireOp",EDGE,"E17.3.2")])],"isStart":false}),makeQuery(id+"F13.opExtrude","SWEPT_FACE",FACE,{"disambiguationData":[OSD([sQuery(id+"F12.wireOp",EDGE,"E17.3.1")])]})],"blendedInto":[makeQuery(id+"F13.opExtrude","SWEPT_FACE",FACE,{"disambiguationData":[OSD([sQuery(id+"F12.wireOp",EDGE,"E17.3.1")])]})]});
            var Q10;
            Q10=makeQuery(id+"F14.opFillet","BLEND_EDGE",EDGE,{"blendedFrom":[makeQuery(id+"F13.opExtrude","CAP_EDGE",EDGE,{"disambiguationData":[OSD([sQuery(id+"F12.wireOp",EDGE,"E17.4.2")])],"isStart":false}),makeQuery(id+"F13.opExtrude","SWEPT_FACE",FACE,{"disambiguationData":[OSD([sQuery(id+"F12.wireOp",EDGE,"E17.4.1")])]})],"blendedInto":[makeQuery(id+"F13.opExtrude","SWEPT_FACE",FACE,{"disambiguationData":[OSD([sQuery(id+"F12.wireOp",EDGE,"E17.4.1")])]})]});
            var Q11;
            Q11=makeQuery(id+"F14.opFillet","BLEND_EDGE",EDGE,{"blendedFrom":[makeQuery(id+"F13.opExtrude","CAP_EDGE",EDGE,{"disambiguationData":[OSD([sQuery(id+"F12.wireOp",EDGE,"E17.5.2")])],"isStart":false}),makeQuery(id+"F13.opExtrude","SWEPT_FACE",FACE,{"disambiguationData":[OSD([sQuery(id+"F12.wireOp",EDGE,"E17.5.1")])]})],"blendedInto":[makeQuery(id+"F13.opExtrude","SWEPT_FACE",FACE,{"disambiguationData":[OSD([sQuery(id+"F12.wireOp",EDGE,"E17.5.1")])]})]});
            var Q12;
            Q12=makeQuery(id+"F14.opFillet","BLEND_EDGE",EDGE,{"blendedFrom":[makeQuery(id+"F13.opExtrude","CAP_EDGE",EDGE,{"disambiguationData":[OSD([sQuery(id+"F12.wireOp",EDGE,"E17.6.2")])],"isStart":false}),makeQuery(id+"F13.opExtrude","SWEPT_FACE",FACE,{"disambiguationData":[OSD([sQuery(id+"F12.wireOp",EDGE,"E17.6.1")])]})],"blendedInto":[makeQuery(id+"F13.opExtrude","SWEPT_FACE",FACE,{"disambiguationData":[OSD([sQuery(id+"F12.wireOp",EDGE,"E17.6.1")])]})]});
            var Q13;
            Q13=makeQuery(id+"F14.opFillet","BLEND_EDGE",EDGE,{"blendedFrom":[makeQuery(id+"F13.opExtrude","CAP_EDGE",EDGE,{"disambiguationData":[OSD([sQuery(id+"F12.wireOp",EDGE,"E17.7.2")])],"isStart":false}),makeQuery(id+"F13.opExtrude","SWEPT_FACE",FACE,{"disambiguationData":[OSD([sQuery(id+"F12.wireOp",EDGE,"E17.7.1")])]})],"blendedInto":[makeQuery(id+"F13.opExtrude","SWEPT_FACE",FACE,{"disambiguationData":[OSD([sQuery(id+"F12.wireOp",EDGE,"E17.7.1")])]})]});
            var Q14;
            Q14=makeQuery(id+"F14.opFillet","BLEND_EDGE",EDGE,{"blendedFrom":[makeQuery(id+"F13.opExtrude","CAP_EDGE",EDGE,{"disambiguationData":[OSD([sQuery(id+"F12.wireOp",EDGE,"E17.8.2")])],"isStart":false}),makeQuery(id+"F13.opExtrude","SWEPT_FACE",FACE,{"disambiguationData":[OSD([sQuery(id+"F12.wireOp",EDGE,"E17.8.1")])]})],"blendedInto":[makeQuery(id+"F13.opExtrude","SWEPT_FACE",FACE,{"disambiguationData":[OSD([sQuery(id+"F12.wireOp",EDGE,"E17.8.1")])]})]});
            var Q15;
            Q15=makeQuery(id+"F14.opFillet","BLEND_EDGE",EDGE,{"blendedFrom":[makeQuery(id+"F13.opExtrude","CAP_EDGE",EDGE,{"disambiguationData":[OSD([sQuery(id+"F12.wireOp",EDGE,"E17.9.2")])],"isStart":false}),makeQuery(id+"F13.opExtrude","SWEPT_FACE",FACE,{"disambiguationData":[OSD([sQuery(id+"F12.wireOp",EDGE,"E17.9.1")])]})],"blendedInto":[makeQuery(id+"F13.opExtrude","SWEPT_FACE",FACE,{"disambiguationData":[OSD([sQuery(id+"F12.wireOp",EDGE,"E17.9.1")])]})]});
            var Q16;
            Q16=makeQuery(id+"F14.opFillet","BLEND_EDGE",EDGE,{"blendedFrom":[makeQuery(id+"F13.opExtrude","CAP_EDGE",EDGE,{"disambiguationData":[OSD([sQuery(id+"F12.wireOp",EDGE,"E17.10.2")])],"isStart":false}),makeQuery(id+"F13.opExtrude","SWEPT_FACE",FACE,{"disambiguationData":[OSD([sQuery(id+"F12.wireOp",EDGE,"E17.10.1")])]})],"blendedInto":[makeQuery(id+"F13.opExtrude","SWEPT_FACE",FACE,{"disambiguationData":[OSD([sQuery(id+"F12.wireOp",EDGE,"E17.10.1")])]})]});
            var Q17;
            Q17=makeQuery(id+"F14.opFillet","BLEND_EDGE",EDGE,{"blendedFrom":[makeQuery(id+"F13.opExtrude","CAP_EDGE",EDGE,{"disambiguationData":[OSD([sQuery(id+"F12.wireOp",EDGE,"E17.11.2")])],"isStart":false}),makeQuery(id+"F13.opExtrude","SWEPT_FACE",FACE,{"disambiguationData":[OSD([sQuery(id+"F12.wireOp",EDGE,"E17.11.1")])]})],"blendedInto":[makeQuery(id+"F13.opExtrude","SWEPT_FACE",FACE,{"disambiguationData":[OSD([sQuery(id+"F12.wireOp",EDGE,"E17.11.1")])]})]});
            var Q18;
            Q18=makeQuery(id+"F14.opFillet","BLEND_EDGE",EDGE,{"blendedFrom":[makeQuery(id+"F13.opExtrude","CAP_EDGE",EDGE,{"disambiguationData":[OSD([sQuery(id+"F12.wireOp",EDGE,"E17.12.2")])],"isStart":false}),makeQuery(id+"F13.opExtrude","SWEPT_FACE",FACE,{"disambiguationData":[OSD([sQuery(id+"F12.wireOp",EDGE,"E17.12.1")])]})],"blendedInto":[makeQuery(id+"F13.opExtrude","SWEPT_FACE",FACE,{"disambiguationData":[OSD([sQuery(id+"F12.wireOp",EDGE,"E17.12.1")])]})]});
            var Q19;
            Q19=makeQuery(id+"F14.opFillet","BLEND_EDGE",EDGE,{"blendedFrom":[makeQuery(id+"F13.opExtrude","CAP_EDGE",EDGE,{"disambiguationData":[OSD([sQuery(id+"F12.wireOp",EDGE,"E17.13.2")])],"isStart":false}),makeQuery(id+"F13.opExtrude","SWEPT_FACE",FACE,{"disambiguationData":[OSD([sQuery(id+"F12.wireOp",EDGE,"E17.13.1")])]})],"blendedInto":[makeQuery(id+"F13.opExtrude","SWEPT_FACE",FACE,{"disambiguationData":[OSD([sQuery(id+"F12.wireOp",EDGE,"E17.13.1")])]})]});
            var Q20;
            Q20=makeQuery(id+"F14.opFillet","BLEND_EDGE",EDGE,{"blendedFrom":[makeQuery(id+"F13.opExtrude","CAP_EDGE",EDGE,{"disambiguationData":[OSD([sQuery(id+"F12.wireOp",EDGE,"E17.14.2")])],"isStart":false}),makeQuery(id+"F13.opExtrude","SWEPT_FACE",FACE,{"disambiguationData":[OSD([sQuery(id+"F12.wireOp",EDGE,"E17.14.1")])]})],"blendedInto":[makeQuery(id+"F13.opExtrude","SWEPT_FACE",FACE,{"disambiguationData":[OSD([sQuery(id+"F12.wireOp",EDGE,"E17.14.1")])]})]});
            var Q21;
            Q21=makeQuery(id+"F14.opFillet","BLEND_EDGE",EDGE,{"blendedFrom":[makeQuery(id+"F13.opExtrude","CAP_EDGE",EDGE,{"disambiguationData":[OSD([sQuery(id+"F12.wireOp",EDGE,"E17.15.2")])],"isStart":false}),makeQuery(id+"F13.opExtrude","SWEPT_FACE",FACE,{"disambiguationData":[OSD([sQuery(id+"F12.wireOp",EDGE,"E17.15.1")])]})],"blendedInto":[makeQuery(id+"F13.opExtrude","SWEPT_FACE",FACE,{"disambiguationData":[OSD([sQuery(id+"F12.wireOp",EDGE,"E17.15.1")])]})]});
            var Q22;
            Q22=makeQuery(id+"F14.opFillet","BLEND_EDGE",EDGE,{"blendedFrom":[makeQuery(id+"F13.opExtrude","CAP_EDGE",EDGE,{"disambiguationData":[OSD([sQuery(id+"F12.wireOp",EDGE,"E17.16.2")])],"isStart":false}),makeQuery(id+"F13.opExtrude","SWEPT_FACE",FACE,{"disambiguationData":[OSD([sQuery(id+"F12.wireOp",EDGE,"E17.16.1")])]})],"blendedInto":[makeQuery(id+"F13.opExtrude","SWEPT_FACE",FACE,{"disambiguationData":[OSD([sQuery(id+"F12.wireOp",EDGE,"E17.16.1")])]})]});
            var Q23;
            Q23=makeQuery(id+"F14.opFillet","BLEND_EDGE",EDGE,{"blendedFrom":[makeQuery(id+"F13.opExtrude","CAP_EDGE",EDGE,{"disambiguationData":[OSD([sQuery(id+"F12.wireOp",EDGE,"E17.17.2")])],"isStart":false}),makeQuery(id+"F13.opExtrude","SWEPT_FACE",FACE,{"disambiguationData":[OSD([sQuery(id+"F12.wireOp",EDGE,"E17.17.1")])]})],"blendedInto":[makeQuery(id+"F13.opExtrude","SWEPT_FACE",FACE,{"disambiguationData":[OSD([sQuery(id+"F12.wireOp",EDGE,"E17.17.1")])]})]});
            var Q24;
            Q24=makeQuery(id+"F14.opFillet","BLEND_EDGE",EDGE,{"blendedFrom":[makeQuery(id+"F13.opExtrude","CAP_EDGE",EDGE,{"disambiguationData":[OSD([sQuery(id+"F12.wireOp",EDGE,"E17.18.2")])],"isStart":false}),makeQuery(id+"F13.opExtrude","SWEPT_FACE",FACE,{"disambiguationData":[OSD([sQuery(id+"F12.wireOp",EDGE,"E17.18.1")])]})],"blendedInto":[makeQuery(id+"F13.opExtrude","SWEPT_FACE",FACE,{"disambiguationData":[OSD([sQuery(id+"F12.wireOp",EDGE,"E17.18.1")])]})]});
            var Q25;
            Q25=makeQuery(id+"F14.opFillet","BLEND_EDGE",EDGE,{"blendedFrom":[makeQuery(id+"F13.opExtrude","CAP_EDGE",EDGE,{"disambiguationData":[OSD([sQuery(id+"F12.wireOp",EDGE,"E17.19.2")])],"isStart":false}),makeQuery(id+"F13.opExtrude","SWEPT_FACE",FACE,{"disambiguationData":[OSD([sQuery(id+"F12.wireOp",EDGE,"E17.19.1")])]})],"blendedInto":[makeQuery(id+"F13.opExtrude","SWEPT_FACE",FACE,{"disambiguationData":[OSD([sQuery(id+"F12.wireOp",EDGE,"E17.19.1")])]})]});
            var Q26;
            Q26=makeQuery(id+"F14.opFillet","BLEND_EDGE",EDGE,{"blendedFrom":[makeQuery(id+"F13.opExtrude","CAP_EDGE",EDGE,{"disambiguationData":[OSD([sQuery(id+"F12.wireOp",EDGE,"E17.20.2")])],"isStart":false}),makeQuery(id+"F13.opExtrude","SWEPT_FACE",FACE,{"disambiguationData":[OSD([sQuery(id+"F12.wireOp",EDGE,"E17.20.1")])]})],"blendedInto":[makeQuery(id+"F13.opExtrude","SWEPT_FACE",FACE,{"disambiguationData":[OSD([sQuery(id+"F12.wireOp",EDGE,"E17.20.1")])]})]});
            var Q27;
            Q27=makeQuery(id+"F14.opFillet","BLEND_EDGE",EDGE,{"blendedFrom":[makeQuery(id+"F13.opExtrude","CAP_EDGE",EDGE,{"disambiguationData":[OSD([sQuery(id+"F12.wireOp",EDGE,"E17.21.2")])],"isStart":false}),makeQuery(id+"F13.opExtrude","SWEPT_FACE",FACE,{"disambiguationData":[OSD([sQuery(id+"F12.wireOp",EDGE,"E17.21.1")])]})],"blendedInto":[makeQuery(id+"F13.opExtrude","SWEPT_FACE",FACE,{"disambiguationData":[OSD([sQuery(id+"F12.wireOp",EDGE,"E17.21.1")])]})]});
            var Q28;
            Q28=makeQuery(id+"F14.opFillet","BLEND_EDGE",EDGE,{"blendedFrom":[makeQuery(id+"F13.opExtrude","CAP_EDGE",EDGE,{"disambiguationData":[OSD([sQuery(id+"F12.wireOp",EDGE,"E17.22.2")])],"isStart":false}),makeQuery(id+"F13.opExtrude","SWEPT_FACE",FACE,{"disambiguationData":[OSD([sQuery(id+"F12.wireOp",EDGE,"E17.22.1")])]})],"blendedInto":[makeQuery(id+"F13.opExtrude","SWEPT_FACE",FACE,{"disambiguationData":[OSD([sQuery(id+"F12.wireOp",EDGE,"E17.22.1")])]})]});
            var Q29;
            Q29=makeQuery(id+"F14.opFillet","BLEND_EDGE",EDGE,{"blendedFrom":[makeQuery(id+"F13.opExtrude","CAP_EDGE",EDGE,{"disambiguationData":[OSD([sQuery(id+"F12.wireOp",EDGE,"E17.23.2")])],"isStart":false}),makeQuery(id+"F13.opExtrude","SWEPT_FACE",FACE,{"disambiguationData":[OSD([sQuery(id+"F12.wireOp",EDGE,"E17.23.1")])]})],"blendedInto":[makeQuery(id+"F13.opExtrude","SWEPT_FACE",FACE,{"disambiguationData":[OSD([sQuery(id+"F12.wireOp",EDGE,"E17.23.1")])]})]});
            var Q30;
            Q30=makeQuery(id+"F14.opFillet","BLEND_EDGE",EDGE,{"blendedFrom":[makeQuery(id+"F13.opExtrude","CAP_EDGE",EDGE,{"disambiguationData":[OSD([sQuery(id+"F12.wireOp",EDGE,"E17.24.2")])],"isStart":false}),makeQuery(id+"F13.opExtrude","SWEPT_FACE",FACE,{"disambiguationData":[OSD([sQuery(id+"F12.wireOp",EDGE,"E17.24.1")])]})],"blendedInto":[makeQuery(id+"F13.opExtrude","SWEPT_FACE",FACE,{"disambiguationData":[OSD([sQuery(id+"F12.wireOp",EDGE,"E17.24.1")])]})]});
            var Q31;
            Q31=makeQuery(id+"F14.opFillet","BLEND_EDGE",EDGE,{"blendedFrom":[makeQuery(id+"F13.opExtrude","CAP_EDGE",EDGE,{"disambiguationData":[OSD([sQuery(id+"F12.wireOp",EDGE,"E17.25.2")])],"isStart":false}),makeQuery(id+"F13.opExtrude","SWEPT_FACE",FACE,{"disambiguationData":[OSD([sQuery(id+"F12.wireOp",EDGE,"E17.25.1")])]})],"blendedInto":[makeQuery(id+"F13.opExtrude","SWEPT_FACE",FACE,{"disambiguationData":[OSD([sQuery(id+"F12.wireOp",EDGE,"E17.25.1")])]})]});
            var Q32;
            Q32=makeQuery(id+"F14.opFillet","BLEND_EDGE",EDGE,{"blendedFrom":[makeQuery(id+"F13.opExtrude","CAP_EDGE",EDGE,{"disambiguationData":[OSD([sQuery(id+"F12.wireOp",EDGE,"E17.26.2")])],"isStart":false}),makeQuery(id+"F13.opExtrude","SWEPT_FACE",FACE,{"disambiguationData":[OSD([sQuery(id+"F12.wireOp",EDGE,"E17.26.1")])]})],"blendedInto":[makeQuery(id+"F13.opExtrude","SWEPT_FACE",FACE,{"disambiguationData":[OSD([sQuery(id+"F12.wireOp",EDGE,"E17.26.1")])]})]});
            var Q33;
            Q33=makeQuery(id+"F14.opFillet","BLEND_EDGE",EDGE,{"blendedFrom":[makeQuery(id+"F13.opExtrude","CAP_EDGE",EDGE,{"disambiguationData":[OSD([sQuery(id+"F12.wireOp",EDGE,"E17.27.2")])],"isStart":false}),makeQuery(id+"F13.opExtrude","SWEPT_FACE",FACE,{"disambiguationData":[OSD([sQuery(id+"F12.wireOp",EDGE,"E17.27.1")])]})],"blendedInto":[makeQuery(id+"F13.opExtrude","SWEPT_FACE",FACE,{"disambiguationData":[OSD([sQuery(id+"F12.wireOp",EDGE,"E17.27.1")])]})]});
            var Q34;
            Q34=makeQuery(id+"F14.opFillet","BLEND_EDGE",EDGE,{"blendedFrom":[makeQuery(id+"F13.opExtrude","CAP_EDGE",EDGE,{"disambiguationData":[OSD([sQuery(id+"F12.wireOp",EDGE,"E17.28.2")])],"isStart":false}),makeQuery(id+"F13.opExtrude","SWEPT_FACE",FACE,{"disambiguationData":[OSD([sQuery(id+"F12.wireOp",EDGE,"E17.28.1")])]})],"blendedInto":[makeQuery(id+"F13.opExtrude","SWEPT_FACE",FACE,{"disambiguationData":[OSD([sQuery(id+"F12.wireOp",EDGE,"E17.28.1")])]})]});
            var Q35;
            Q35=makeQuery(id+"F14.opFillet","BLEND_EDGE",EDGE,{"blendedFrom":[makeQuery(id+"F13.opExtrude","CAP_EDGE",EDGE,{"disambiguationData":[OSD([sQuery(id+"F12.wireOp",EDGE,"E17.29.2")])],"isStart":false}),makeQuery(id+"F13.opExtrude","SWEPT_FACE",FACE,{"disambiguationData":[OSD([sQuery(id+"F12.wireOp",EDGE,"E17.29.1")])]})],"blendedInto":[makeQuery(id+"F13.opExtrude","SWEPT_FACE",FACE,{"disambiguationData":[OSD([sQuery(id+"F12.wireOp",EDGE,"E17.29.1")])]})]});
            var Q36;
            Q36=makeQuery(id+"F13.opExtrude","SWEPT_FACE",FACE,{"disambiguationData":[OSD([sQuery(id+"F12.wireOp",EDGE,"E17.1.1")])]});
            var Q37;
            Q37=makeQuery(id+"F13.opExtrude","SWEPT_FACE",FACE,{"disambiguationData":[OSD([sQuery(id+"F12.wireOp",EDGE,"E17.2.1")])]});
            var Q38;
            Q38=makeQuery(id+"F13.opExtrude","SWEPT_FACE",FACE,{"disambiguationData":[OSD([sQuery(id+"F12.wireOp",EDGE,"E17.3.1")])]});
            var Q39;
            Q39=makeQuery(id+"F13.opExtrude","SWEPT_FACE",FACE,{"disambiguationData":[OSD([sQuery(id+"F12.wireOp",EDGE,"E17.4.1")])]});
            var Q40;
            Q40=makeQuery(id+"F13.opExtrude","SWEPT_FACE",FACE,{"disambiguationData":[OSD([sQuery(id+"F12.wireOp",EDGE,"E17.5.1")])]});
            var Q41;
            Q41=makeQuery(id+"F14.opFillet","BLEND_EDGE",EDGE,{"blendedFrom":[makeQuery(id+"F13.opExtrude","CAP_EDGE",EDGE,{"disambiguationData":[OSD([sQuery(id+"F12.wireOp",EDGE,"E17.35.0")])],"isStart":false}),makeQuery(id+"F13.opExtrude","SWEPT_FACE",FACE,{"disambiguationData":[OSD([sQuery(id+"F12.wireOp",EDGE,"E17.35.1")])]})],"blendedInto":[makeQuery(id+"F13.opExtrude","SWEPT_FACE",FACE,{"disambiguationData":[OSD([sQuery(id+"F12.wireOp",EDGE,"E17.35.1")])]})]});
            var Q42;
            Q42=makeQuery(id+"F14.opFillet","BLEND_EDGE",EDGE,{"blendedFrom":[makeQuery(id+"F13.opExtrude","CAP_EDGE",EDGE,{"disambiguationData":[OSD([sQuery(id+"F12.wireOp",EDGE,"E17.34.0")])],"isStart":false}),makeQuery(id+"F13.opExtrude","SWEPT_FACE",FACE,{"disambiguationData":[OSD([sQuery(id+"F12.wireOp",EDGE,"E17.34.1")])]})],"blendedInto":[makeQuery(id+"F13.opExtrude","SWEPT_FACE",FACE,{"disambiguationData":[OSD([sQuery(id+"F12.wireOp",EDGE,"E17.34.1")])]})]});
            var Q43;
            Q43=makeQuery(id+"F14.opFillet","BLEND_EDGE",EDGE,{"blendedFrom":[makeQuery(id+"F13.opExtrude","CAP_EDGE",EDGE,{"disambiguationData":[OSD([sQuery(id+"F12.wireOp",EDGE,"E17.33.0")])],"isStart":false}),makeQuery(id+"F13.opExtrude","SWEPT_FACE",FACE,{"disambiguationData":[OSD([sQuery(id+"F12.wireOp",EDGE,"E17.33.1")])]})],"blendedInto":[makeQuery(id+"F13.opExtrude","SWEPT_FACE",FACE,{"disambiguationData":[OSD([sQuery(id+"F12.wireOp",EDGE,"E17.33.1")])]})]});
            var Q44;
            Q44=makeQuery(id+"F14.opFillet","BLEND_EDGE",EDGE,{"blendedFrom":[makeQuery(id+"F13.opExtrude","CAP_EDGE",EDGE,{"disambiguationData":[OSD([sQuery(id+"F12.wireOp",EDGE,"E17.32.0")])],"isStart":false}),makeQuery(id+"F13.opExtrude","SWEPT_FACE",FACE,{"disambiguationData":[OSD([sQuery(id+"F12.wireOp",EDGE,"E17.32.1")])]})],"blendedInto":[makeQuery(id+"F13.opExtrude","SWEPT_FACE",FACE,{"disambiguationData":[OSD([sQuery(id+"F12.wireOp",EDGE,"E17.32.1")])]})]});
            var Q45;
            Q45=makeQuery(id+"F14.opFillet","BLEND_EDGE",EDGE,{"blendedFrom":[makeQuery(id+"F13.opExtrude","CAP_EDGE",EDGE,{"disambiguationData":[OSD([sQuery(id+"F12.wireOp",EDGE,"E17.31.0")])],"isStart":false}),makeQuery(id+"F13.opExtrude","SWEPT_FACE",FACE,{"disambiguationData":[OSD([sQuery(id+"F12.wireOp",EDGE,"E17.31.1")])]})],"blendedInto":[makeQuery(id+"F13.opExtrude","SWEPT_FACE",FACE,{"disambiguationData":[OSD([sQuery(id+"F12.wireOp",EDGE,"E17.31.1")])]})]});
            var Q46;
            Q46=makeQuery(id+"F14.opFillet","BLEND_EDGE",EDGE,{"blendedFrom":[makeQuery(id+"F13.opExtrude","CAP_EDGE",EDGE,{"disambiguationData":[OSD([sQuery(id+"F12.wireOp",EDGE,"E17.30.0")])],"isStart":false}),makeQuery(id+"F13.opExtrude","SWEPT_FACE",FACE,{"disambiguationData":[OSD([sQuery(id+"F12.wireOp",EDGE,"E17.30.1")])]})],"blendedInto":[makeQuery(id+"F13.opExtrude","SWEPT_FACE",FACE,{"disambiguationData":[OSD([sQuery(id+"F12.wireOp",EDGE,"E17.30.1")])]})]});
            var Q47;
            Q47=makeQuery(id+"F13.opExtrude","SWEPT_FACE",FACE,{"disambiguationData":[OSD([sQuery(id+"F12.wireOp",EDGE,"E17.6.1")])]});
            var Q48;
            Q48=makeQuery(id+"F13.opExtrude","SWEPT_FACE",FACE,{"disambiguationData":[OSD([sQuery(id+"F12.wireOp",EDGE,"E17.7.1")])]});
            var Q49;
            Q49=makeQuery(id+"F13.opExtrude","SWEPT_FACE",FACE,{"disambiguationData":[OSD([sQuery(id+"F12.wireOp",EDGE,"E17.8.1")])]});
            var Q50;
            Q50=makeQuery(id+"F13.opExtrude","SWEPT_FACE",FACE,{"disambiguationData":[OSD([sQuery(id+"F12.wireOp",EDGE,"E17.9.1")])]});
            var Q51;
            Q51=makeQuery(id+"F14.opFillet","BLEND_EDGE",EDGE,{"blendedFrom":[makeQuery(id+"F13.opExtrude","CAP_EDGE",EDGE,{"disambiguationData":[OSD([sQuery(id+"F12.wireOp",EDGE,"E17.10.0")])],"isStart":false}),makeQuery(id+"F13.opExtrude","SWEPT_FACE",FACE,{"disambiguationData":[OSD([sQuery(id+"F12.wireOp",EDGE,"E17.10.1")])]})],"blendedInto":[makeQuery(id+"F13.opExtrude","SWEPT_FACE",FACE,{"disambiguationData":[OSD([sQuery(id+"F12.wireOp",EDGE,"E17.10.1")])]})]});
            var Q52;
            Q52=makeQuery(id+"F14.opFillet","BLEND_EDGE",EDGE,{"blendedFrom":[makeQuery(id+"F13.opExtrude","CAP_EDGE",EDGE,{"disambiguationData":[OSD([sQuery(id+"F12.wireOp",EDGE,"E17.11.0")])],"isStart":false}),makeQuery(id+"F13.opExtrude","SWEPT_FACE",FACE,{"disambiguationData":[OSD([sQuery(id+"F12.wireOp",EDGE,"E17.11.1")])]})],"blendedInto":[makeQuery(id+"F13.opExtrude","SWEPT_FACE",FACE,{"disambiguationData":[OSD([sQuery(id+"F12.wireOp",EDGE,"E17.11.1")])]})]});
            var Q53;
            Q53=makeQuery(id+"F13.opExtrude","SWEPT_FACE",FACE,{"disambiguationData":[OSD([sQuery(id+"F12.wireOp",EDGE,"E17.12.1")])]});
            var Q54;
            Q54=makeQuery(id+"F13.opExtrude","SWEPT_FACE",FACE,{"disambiguationData":[OSD([sQuery(id+"F12.wireOp",EDGE,"E17.13.1")])]});
            var Q55;
            Q55=makeQuery(id+"F13.opExtrude","SWEPT_FACE",FACE,{"disambiguationData":[OSD([sQuery(id+"F12.wireOp",EDGE,"E17.14.1")])]});
            var Q56;
            Q56=makeQuery(id+"F14.opFillet","BLEND_EDGE",EDGE,{"blendedFrom":[makeQuery(id+"F13.opExtrude","CAP_EDGE",EDGE,{"disambiguationData":[OSD([sQuery(id+"F12.wireOp",EDGE,"E17.15.0")])],"isStart":false}),makeQuery(id+"F13.opExtrude","SWEPT_FACE",FACE,{"disambiguationData":[OSD([sQuery(id+"F12.wireOp",EDGE,"E17.15.1")])]})],"blendedInto":[makeQuery(id+"F13.opExtrude","SWEPT_FACE",FACE,{"disambiguationData":[OSD([sQuery(id+"F12.wireOp",EDGE,"E17.15.1")])]})]});
            var Q57;
            Q57=makeQuery(id+"F13.opExtrude","SWEPT_FACE",FACE,{"disambiguationData":[OSD([sQuery(id+"F12.wireOp",EDGE,"E17.16.1")])]});
            var Q58;
            Q58=makeQuery(id+"F13.opExtrude","SWEPT_FACE",FACE,{"disambiguationData":[OSD([sQuery(id+"F12.wireOp",EDGE,"E17.17.1")])]});
            var Q59;
            Q59=makeQuery(id+"F14.opFillet","BLEND_EDGE",EDGE,{"blendedFrom":[makeQuery(id+"F13.opExtrude","CAP_EDGE",EDGE,{"disambiguationData":[OSD([sQuery(id+"F12.wireOp",EDGE,"E17.18.0")])],"isStart":false}),makeQuery(id+"F13.opExtrude","SWEPT_FACE",FACE,{"disambiguationData":[OSD([sQuery(id+"F12.wireOp",EDGE,"E17.18.1")])]})],"blendedInto":[makeQuery(id+"F13.opExtrude","SWEPT_FACE",FACE,{"disambiguationData":[OSD([sQuery(id+"F12.wireOp",EDGE,"E17.18.1")])]})]});
            var Q60;
            Q60=makeQuery(id+"F14.opFillet","BLEND_EDGE",EDGE,{"blendedFrom":[makeQuery(id+"F13.opExtrude","CAP_EDGE",EDGE,{"disambiguationData":[OSD([sQuery(id+"F12.wireOp",EDGE,"E17.19.0")])],"isStart":false}),makeQuery(id+"F13.opExtrude","SWEPT_FACE",FACE,{"disambiguationData":[OSD([sQuery(id+"F12.wireOp",EDGE,"E17.19.1")])]})],"blendedInto":[makeQuery(id+"F13.opExtrude","SWEPT_FACE",FACE,{"disambiguationData":[OSD([sQuery(id+"F12.wireOp",EDGE,"E17.19.1")])]})]});
            var Q61;
            Q61=makeQuery(id+"F14.opFillet","BLEND_EDGE",EDGE,{"blendedFrom":[makeQuery(id+"F13.opExtrude","CAP_EDGE",EDGE,{"disambiguationData":[OSD([sQuery(id+"F12.wireOp",EDGE,"E17.20.0")])],"isStart":false}),makeQuery(id+"F13.opExtrude","SWEPT_FACE",FACE,{"disambiguationData":[OSD([sQuery(id+"F12.wireOp",EDGE,"E17.20.1")])]})],"blendedInto":[makeQuery(id+"F13.opExtrude","SWEPT_FACE",FACE,{"disambiguationData":[OSD([sQuery(id+"F12.wireOp",EDGE,"E17.20.1")])]})]});
            var Q62;
            Q62=makeQuery(id+"F14.opFillet","BLEND_EDGE",EDGE,{"blendedFrom":[makeQuery(id+"F13.opExtrude","CAP_EDGE",EDGE,{"disambiguationData":[OSD([sQuery(id+"F12.wireOp",EDGE,"E17.21.0")])],"isStart":false}),makeQuery(id+"F13.opExtrude","SWEPT_FACE",FACE,{"disambiguationData":[OSD([sQuery(id+"F12.wireOp",EDGE,"E17.21.1")])]})],"blendedInto":[makeQuery(id+"F13.opExtrude","SWEPT_FACE",FACE,{"disambiguationData":[OSD([sQuery(id+"F12.wireOp",EDGE,"E17.21.1")])]})]});
            var Q63;
            Q63=makeQuery(id+"F14.opFillet","BLEND_EDGE",EDGE,{"blendedFrom":[makeQuery(id+"F13.opExtrude","CAP_EDGE",EDGE,{"disambiguationData":[OSD([sQuery(id+"F12.wireOp",EDGE,"E17.22.0")])],"isStart":false}),makeQuery(id+"F13.opExtrude","SWEPT_FACE",FACE,{"disambiguationData":[OSD([sQuery(id+"F12.wireOp",EDGE,"E17.22.1")])]})],"blendedInto":[makeQuery(id+"F13.opExtrude","SWEPT_FACE",FACE,{"disambiguationData":[OSD([sQuery(id+"F12.wireOp",EDGE,"E17.22.1")])]})]});
            var Q64;
            Q64=makeQuery(id+"F14.opFillet","BLEND_EDGE",EDGE,{"blendedFrom":[makeQuery(id+"F13.opExtrude","CAP_EDGE",EDGE,{"disambiguationData":[OSD([sQuery(id+"F12.wireOp",EDGE,"E17.23.0")])],"isStart":false}),makeQuery(id+"F13.opExtrude","SWEPT_FACE",FACE,{"disambiguationData":[OSD([sQuery(id+"F12.wireOp",EDGE,"E17.23.1")])]})],"blendedInto":[makeQuery(id+"F13.opExtrude","SWEPT_FACE",FACE,{"disambiguationData":[OSD([sQuery(id+"F12.wireOp",EDGE,"E17.23.1")])]})]});
            var Q65;
            Q65=makeQuery(id+"F14.opFillet","BLEND_EDGE",EDGE,{"blendedFrom":[makeQuery(id+"F13.opExtrude","CAP_EDGE",EDGE,{"disambiguationData":[OSD([sQuery(id+"F12.wireOp",EDGE,"E17.24.0")])],"isStart":false}),makeQuery(id+"F13.opExtrude","SWEPT_FACE",FACE,{"disambiguationData":[OSD([sQuery(id+"F12.wireOp",EDGE,"E17.24.1")])]})],"blendedInto":[makeQuery(id+"F13.opExtrude","SWEPT_FACE",FACE,{"disambiguationData":[OSD([sQuery(id+"F12.wireOp",EDGE,"E17.24.1")])]})]});
            var Q66;
            Q66=makeQuery(id+"F14.opFillet","BLEND_EDGE",EDGE,{"blendedFrom":[makeQuery(id+"F13.opExtrude","CAP_EDGE",EDGE,{"disambiguationData":[OSD([sQuery(id+"F12.wireOp",EDGE,"E17.25.0")])],"isStart":false}),makeQuery(id+"F13.opExtrude","SWEPT_FACE",FACE,{"disambiguationData":[OSD([sQuery(id+"F12.wireOp",EDGE,"E17.25.1")])]})],"blendedInto":[makeQuery(id+"F13.opExtrude","SWEPT_FACE",FACE,{"disambiguationData":[OSD([sQuery(id+"F12.wireOp",EDGE,"E17.25.1")])]})]});
            var Q67;
            Q67=makeQuery(id+"F14.opFillet","BLEND_EDGE",EDGE,{"blendedFrom":[makeQuery(id+"F13.opExtrude","CAP_EDGE",EDGE,{"disambiguationData":[OSD([sQuery(id+"F12.wireOp",EDGE,"E17.26.0")])],"isStart":false}),makeQuery(id+"F13.opExtrude","SWEPT_FACE",FACE,{"disambiguationData":[OSD([sQuery(id+"F12.wireOp",EDGE,"E17.26.1")])]})],"blendedInto":[makeQuery(id+"F13.opExtrude","SWEPT_FACE",FACE,{"disambiguationData":[OSD([sQuery(id+"F12.wireOp",EDGE,"E17.26.1")])]})]});
            var Q68;
            Q68=makeQuery(id+"F14.opFillet","BLEND_EDGE",EDGE,{"blendedFrom":[makeQuery(id+"F13.opExtrude","CAP_EDGE",EDGE,{"disambiguationData":[OSD([sQuery(id+"F12.wireOp",EDGE,"E17.27.0")])],"isStart":false}),makeQuery(id+"F13.opExtrude","SWEPT_FACE",FACE,{"disambiguationData":[OSD([sQuery(id+"F12.wireOp",EDGE,"E17.27.1")])]})],"blendedInto":[makeQuery(id+"F13.opExtrude","SWEPT_FACE",FACE,{"disambiguationData":[OSD([sQuery(id+"F12.wireOp",EDGE,"E17.27.1")])]})]});
            var Q69;
            Q69=makeQuery(id+"F14.opFillet","BLEND_EDGE",EDGE,{"blendedFrom":[makeQuery(id+"F13.opExtrude","CAP_EDGE",EDGE,{"disambiguationData":[OSD([sQuery(id+"F12.wireOp",EDGE,"E17.28.0")])],"isStart":false}),makeQuery(id+"F13.opExtrude","SWEPT_FACE",FACE,{"disambiguationData":[OSD([sQuery(id+"F12.wireOp",EDGE,"E17.28.1")])]})],"blendedInto":[makeQuery(id+"F13.opExtrude","SWEPT_FACE",FACE,{"disambiguationData":[OSD([sQuery(id+"F12.wireOp",EDGE,"E17.28.1")])]})]});
            var Q70;
            Q70=makeQuery(id+"F14.opFillet","BLEND_EDGE",EDGE,{"blendedFrom":[makeQuery(id+"F13.opExtrude","CAP_EDGE",EDGE,{"disambiguationData":[OSD([sQuery(id+"F12.wireOp",EDGE,"E17.29.0")])],"isStart":false}),makeQuery(id+"F13.opExtrude","SWEPT_FACE",FACE,{"disambiguationData":[OSD([sQuery(id+"F12.wireOp",EDGE,"E17.29.1")])]})],"blendedInto":[makeQuery(id+"F13.opExtrude","SWEPT_FACE",FACE,{"disambiguationData":[OSD([sQuery(id+"F12.wireOp",EDGE,"E17.29.1")])]})]});
            fillet(context, id + "F15", {"entities" : qUnion([Q0, Q1, Q2, Q3, Q4, Q5, Q6, Q7, Q8, Q9, Q10, Q11, Q12, Q13, Q14, Q15, Q16, Q17, Q18, Q19, Q20, Q21, Q22, Q23, Q24, Q25, Q26, Q27, Q28, Q29, Q30, Q31, Q32, Q33, Q34, Q35, Q36, Q37, Q38, Q39, Q40, Q41, Q42, Q43, Q44, Q45, Q46, Q47, Q48, Q49, Q50, Q51, Q52, Q53, Q54, Q55, Q56, Q57, Q58, Q59, Q60, Q61, Q62, Q63, Q64, Q65, Q66, Q67, Q68, Q69, Q70]), "radius" : 2.67 * mm, "tangentPropagation" : true, "allowEdgeOverflow" : false});
        }
        {
            var Q0;
            Q0=makeQuery(id+"F9.opExtrude","CAP_FACE",FACE,{"disambiguationData":[OSD([sQuery(id+"F8.wireOp",EDGE,"E15")])],"isStart":false});
            var Q1;
            Q1=makeQuery(id+"F7.opExtrude","CAP_EDGE",EDGE,{"disambiguationData":[OSD([sQuery(id+"F6.wireOp",EDGE,"E14")])],"isStart":false});
            chamfer(context, id + "F16", {"entities" : qUnion([Q0, Q1]), "chamferType" : ChamferType.TWO_OFFSETS, "width1" : 0.64 * mm, "oppositeDirection" : false, "width2" : 7.62 * mm, "tangentPropagation" : true});
        }
        {
            var Q0;
            {var subQ0=sQuery(id+"F8.wireOp",EDGE,"E15");Q0=makeQuery(id+"F16.opChamfer","BLEND_EDGE",EDGE,{"blendedFrom":[makeQuery(id+"F9.opExtrude","CAP_EDGE",EDGE,{"disambiguationData":[OSD([subQ0])],"isStart":false}),makeQuery(id+"F9.opExtrude","CAP_FACE",FACE,{"disambiguationData":[OSD([subQ0])],"isStart":false})],"blendedInto":[makeQuery(id+"F9.opExtrude","CAP_FACE",FACE,{"disambiguationData":[OSD([subQ0])],"isStart":false})]});}
            var Q1;
            {var subQ0=sQuery(id+"F6.wireOp",EDGE,"E14");Q1=makeQuery(id+"F16.opChamfer","BLEND_EDGE",EDGE,{"blendedFrom":[makeQuery(id+"F7.opExtrude","CAP_EDGE",EDGE,{"disambiguationData":[OSD([subQ0])],"isStart":false}),makeQuery(id+"F7.opExtrude","CAP_FACE",FACE,{"disambiguationData":[OSD([subQ0])],"isStart":false})],"blendedInto":[makeQuery(id+"F7.opExtrude","CAP_FACE",FACE,{"disambiguationData":[OSD([subQ0])],"isStart":false})]});}
            var Q2;
            {var subQ0=sQuery(id+"F8.wireOp",EDGE,"E15");Q2=makeQuery(id+"F16.opChamfer","BLEND_EDGE",EDGE,{"blendedFrom":[makeQuery(id+"F9.opExtrude","CAP_EDGE",EDGE,{"disambiguationData":[OSD([subQ0])],"isStart":false}),makeQuery(id+"F9.opExtrude","SWEPT_FACE",FACE,{"disambiguationData":[OSD([subQ0])]})],"blendedInto":[makeQuery(id+"F9.opExtrude","SWEPT_FACE",FACE,{"disambiguationData":[OSD([subQ0])]})]});}
            var Q3;
            {var subQ0=sQuery(id+"F6.wireOp",EDGE,"E14");Q3=makeQuery(id+"F16.opChamfer","BLEND_EDGE",EDGE,{"blendedFrom":[makeQuery(id+"F7.opExtrude","CAP_EDGE",EDGE,{"disambiguationData":[OSD([subQ0])],"isStart":false}),makeQuery(id+"F7.opExtrude","SWEPT_FACE",FACE,{"disambiguationData":[OSD([subQ0])]})],"blendedInto":[makeQuery(id+"F7.opExtrude","SWEPT_FACE",FACE,{"disambiguationData":[OSD([subQ0])]})]});}
            fillet(context, id + "F17", {"entities" : qUnion([Q0, Q1, Q2, Q3]), "radius" : 0.64 * mm, "tangentPropagation" : true, "allowEdgeOverflow" : false});
        }
        {
            var Q0;
            Q0=qCreatedBy(makeId("Right.planeOp"),FACE);
            var sketch = newSketch(context, id + "F18", { "sketchPlane" : qUnion([Q0])});
            skLineSegment(sketch, "E18.bottom", {"start": v(-92.96, 3.17) * mm, "end": v(-86.61, 3.17) * mm});
            skLineSegment(sketch, "E18.top", {"start": v(-92.96, -3.18) * mm, "end": v(-86.61, -3.18) * mm});
            skLineSegment(sketch, "E18.left", {"start": v(-92.96, 3.17) * mm, "end": v(-92.96, -3.18) * mm});
            skLineSegment(sketch, "E18.right", {"start": v(-86.61, 3.17) * mm, "end": v(-86.61, -3.18) * mm});
            skPoint(sketch, "E18.middle", {"position": v(-89.79, 0) * mm});
            skSolve(sketch);
        }
        {
            var Q0;
            Q0 = qSketchRegion(id + "F18", true);
            extrude(context, id + "F19", {"entities" : qUnion([Q0]), "operationType" : NewBodyOperationType.REMOVE, "depth" : 25.4 * mm});
        }
        {
            var Q0;
            Q0=makeQuery(id+"F19.boolean.opBoolean","COPY",FACE,{"derivedFrom":makeQuery(id+"F19.opExtrude","CAP_FACE",FACE,{"disambiguationData":[OSD([sQuery(id+"F18.wireOp",EDGE,"E18.bottom"),sQuery(id+"F18.wireOp",EDGE,"E18.top"),sQuery(id+"F18.wireOp",EDGE,"E18.left"),sQuery(id+"F18.wireOp",EDGE,"E18.right")])],"isStart":true})});
            extrude(context, id + "F20", {"entities" : qUnion([Q0]), "operationType" : NewBodyOperationType.REMOVE, "oppositeDirection" : true, "depth" : 1.8 * mm});
        }
        {
            var Q0;
            {var subQ0=sQuery(id+"F18.wireOp",EDGE,"E18.left");var subQ1=sQuery(id+"F18.wireOp",EDGE,"E18.top");Q0=makeQuery(id+"F20.boolean.opBoolean","MERGE",EDGE,{"derivedFrom":[makeQuery(id+"F19.boolean.opBoolean","COPY",EDGE,{"derivedFrom":makeQuery(id+"F19.opExtrude","SWEPT_EDGE",EDGE,{"disambiguationData":[OSD([subQ1,subQ0])]})}),makeQuery(id+"F20.opExtrude","SWEPT_EDGE",EDGE,{"disambiguationData":[OSD([subQ1,subQ0])]})]});}
            var Q1;
            {var subQ0=sQuery(id+"F18.wireOp",EDGE,"E18.right");var subQ1=sQuery(id+"F18.wireOp",EDGE,"E18.top");Q1=makeQuery(id+"F20.boolean.opBoolean","MERGE",EDGE,{"derivedFrom":[makeQuery(id+"F19.boolean.opBoolean","COPY",EDGE,{"derivedFrom":makeQuery(id+"F19.opExtrude","SWEPT_EDGE",EDGE,{"disambiguationData":[OSD([subQ1,subQ0])]})}),makeQuery(id+"F20.opExtrude","SWEPT_EDGE",EDGE,{"disambiguationData":[OSD([subQ1,subQ0])]})]});}
            var Q2;
            {var subQ0=sQuery(id+"F18.wireOp",EDGE,"E18.right");var subQ1=sQuery(id+"F18.wireOp",EDGE,"E18.bottom");Q2=makeQuery(id+"F20.boolean.opBoolean","MERGE",EDGE,{"derivedFrom":[makeQuery(id+"F19.boolean.opBoolean","COPY",EDGE,{"derivedFrom":makeQuery(id+"F19.opExtrude","SWEPT_EDGE",EDGE,{"disambiguationData":[OSD([subQ1,subQ0])]})}),makeQuery(id+"F20.opExtrude","SWEPT_EDGE",EDGE,{"disambiguationData":[OSD([subQ1,subQ0])]})]});}
            var Q3;
            {var subQ0=sQuery(id+"F18.wireOp",EDGE,"E18.left");var subQ1=sQuery(id+"F18.wireOp",EDGE,"E18.bottom");Q3=makeQuery(id+"F20.boolean.opBoolean","MERGE",EDGE,{"derivedFrom":[makeQuery(id+"F19.boolean.opBoolean","COPY",EDGE,{"derivedFrom":makeQuery(id+"F19.opExtrude","SWEPT_EDGE",EDGE,{"disambiguationData":[OSD([subQ1,subQ0])]})}),makeQuery(id+"F20.opExtrude","SWEPT_EDGE",EDGE,{"disambiguationData":[OSD([subQ1,subQ0])]})]});}
            var Q4;
            Q4=makeQuery(id+"F20.boolean.opBoolean","COPY",FACE,{"derivedFrom":makeQuery(id+"F20.opExtrude","CAP_FACE",FACE,{"disambiguationData":[OSD([sQuery(id+"F18.wireOp",EDGE,"E18.bottom"),sQuery(id+"F18.wireOp",EDGE,"E18.top"),sQuery(id+"F18.wireOp",EDGE,"E18.left"),sQuery(id+"F18.wireOp",EDGE,"E18.right")])],"isStart":false})});
            fillet(context, id + "F21", {"entities" : qUnion([Q0, Q1, Q2, Q3, Q4]), "radius" : 1.27 * mm, "tangentPropagation" : true, "allowEdgeOverflow" : false});
        }
        {
            var Q0;
            Q0=makeQuery(id+"F20.boolean.opBoolean","COPY",FACE,{"derivedFrom":makeQuery(id+"F20.opExtrude","CAP_FACE",FACE,{"disambiguationData":[OSD([sQuery(id+"F18.wireOp",EDGE,"E18.bottom"),sQuery(id+"F18.wireOp",EDGE,"E18.top"),sQuery(id+"F18.wireOp",EDGE,"E18.left"),sQuery(id+"F18.wireOp",EDGE,"E18.right")])],"isStart":false})});
            var sketch = newSketch(context, id + "F22", { "sketchPlane" : qUnion([Q0])});
            skLineSegment(sketch, "E19.bottom", {"start": v(-89.15, 5.71) * mm, "end": v(-90.42, 5.71) * mm});
            skLineSegment(sketch, "E19.top", {"start": v(-89.15, 13.33) * mm, "end": v(-90.42, 13.33) * mm});
            skLineSegment(sketch, "E19.left", {"start": v(-89.15, 5.71) * mm, "end": v(-89.15, 13.33) * mm});
            skLineSegment(sketch, "E19.right", {"start": v(-90.42, 5.71) * mm, "end": v(-90.42, 13.33) * mm});
            skPoint(sketch, "E19.middle", {"position": v(-89.79, 9.52) * mm});
            skPoint(sketch, "E19.middle.positionSnap0", {"position": v(-89.79, 1.9) * mm});
            skPoint(sketch, "E19.centerSnap0", {"position": v(-89.79, 1.9) * mm});
            skLineSegment(sketch, "E20.bottom", {"start": v(-89.15, -5.72) * mm, "end": v(-90.42, -5.72) * mm});
            skLineSegment(sketch, "E20.top", {"start": v(-89.15, -13.34) * mm, "end": v(-90.42, -13.34) * mm});
            skLineSegment(sketch, "E20.left", {"start": v(-89.15, -5.72) * mm, "end": v(-89.15, -13.34) * mm});
            skLineSegment(sketch, "E20.right", {"start": v(-90.42, -5.72) * mm, "end": v(-90.42, -13.34) * mm});
            skPoint(sketch, "E20.middle", {"position": v(-89.79, -9.53) * mm});
            skPoint(sketch, "E20.middle.positionSnap0", {"position": v(-89.79, -1.9) * mm});
            skPoint(sketch, "E20.centerSnap0", {"position": v(-89.79, -1.9) * mm});
            skSolve(sketch);
        }
        {
            var Q0;
            Q0 = qSketchRegion(id + "F22", true);
            extrude(context, id + "F23", {"entities" : qUnion([Q0]), "operationType" : NewBodyOperationType.ADD, "depth" : 31.75 * mm});
        }
        {
            var Q0;
            Q0=makeQuery(id+"F23.opExtrude","CAP_FACE",FACE,{"disambiguationData":[OSD([sQuery(id+"F22.wireOp",EDGE,"E19.bottom"),sQuery(id+"F22.wireOp",EDGE,"E19.top"),sQuery(id+"F22.wireOp",EDGE,"E19.left"),sQuery(id+"F22.wireOp",EDGE,"E19.right")])],"isStart":false});
            var Q1;
            Q1=makeQuery(id+"F23.opExtrude","SWEPT_EDGE",EDGE,{"disambiguationData":[OSD([sQuery(id+"F22.wireOp",EDGE,"E19.top"),sQuery(id+"F22.wireOp",EDGE,"E19.right")])]});
            var Q2;
            Q2=makeQuery(id+"F23.opExtrude","SWEPT_EDGE",EDGE,{"disambiguationData":[OSD([sQuery(id+"F22.wireOp",EDGE,"E19.top"),sQuery(id+"F22.wireOp",EDGE,"E19.left")])]});
            var Q3;
            Q3=makeQuery(id+"F23.opExtrude","SWEPT_EDGE",EDGE,{"disambiguationData":[OSD([sQuery(id+"F22.wireOp",EDGE,"E19.bottom"),sQuery(id+"F22.wireOp",EDGE,"E19.right")])]});
            var Q4;
            Q4=makeQuery(id+"F23.opExtrude","CAP_FACE",FACE,{"disambiguationData":[OSD([sQuery(id+"F22.wireOp",EDGE,"E20.bottom"),sQuery(id+"F22.wireOp",EDGE,"E20.top"),sQuery(id+"F22.wireOp",EDGE,"E20.left"),sQuery(id+"F22.wireOp",EDGE,"E20.right")])],"isStart":false});
            var Q5;
            Q5=makeQuery(id+"F23.opExtrude","SWEPT_EDGE",EDGE,{"disambiguationData":[OSD([sQuery(id+"F22.wireOp",EDGE,"E20.bottom"),sQuery(id+"F22.wireOp",EDGE,"E20.right")])]});
            var Q6;
            Q6=makeQuery(id+"F23.opExtrude","SWEPT_EDGE",EDGE,{"disambiguationData":[OSD([sQuery(id+"F22.wireOp",EDGE,"E20.bottom"),sQuery(id+"F22.wireOp",EDGE,"E20.left")])]});
            var Q7;
            Q7=makeQuery(id+"F23.opExtrude","SWEPT_EDGE",EDGE,{"disambiguationData":[OSD([sQuery(id+"F22.wireOp",EDGE,"E20.top"),sQuery(id+"F22.wireOp",EDGE,"E20.right")])]});
            var Q8;
            Q8=makeQuery(id+"F23.opExtrude","SWEPT_EDGE",EDGE,{"disambiguationData":[OSD([sQuery(id+"F22.wireOp",EDGE,"E19.bottom"),sQuery(id+"F22.wireOp",EDGE,"E19.left")])]});
            var Q9;
            Q9=makeQuery(id+"F23.opExtrude","SWEPT_EDGE",EDGE,{"disambiguationData":[OSD([sQuery(id+"F22.wireOp",EDGE,"E20.top"),sQuery(id+"F22.wireOp",EDGE,"E20.left")])]});
            fillet(context, id + "F24", {"entities" : qUnion([Q0, Q1, Q2, Q3, Q4, Q5, Q6, Q7, Q8, Q9]), "radius" : 0.64 * mm, "tangentPropagation" : true, "allowEdgeOverflow" : false});
        }
        {
            var Q0;
            Q0=qCreatedBy(makeId("Front.planeOp"),FACE);
            var sketch = newSketch(context, id + "F25", { "sketchPlane" : qUnion([Q0])});
            skLineSegment(sketch, "E21.bottom", {"start": v(75.26, 76.45) * mm, "end": v(0, 76.45) * mm});
            skLineSegment(sketch, "E21.top", {"start": v(75.26, -76.45) * mm, "end": v(0, -76.45) * mm});
            skLineSegment(sketch, "E21.left", {"start": v(0, 76.45) * mm, "end": v(0, -76.45) * mm});
            skLineSegment(sketch, "E21.right", {"start": v(75.26, 76.45) * mm, "end": v(75.26, -76.45) * mm});
            skSolve(sketch);
        }
        {
            var Q0;
            Q0 = qSketchRegion(id + "F25", true);
            extrude(context, id + "F26", {"entities" : qUnion([Q0]), "operationType" : NewBodyOperationType.REMOVE, "endBound" : BoundingType.SYMMETRIC, "oppositeDirection" : true, "depth" : 304.8 * mm});
        }
        {
            var Q0;
            Q0=makeQuery(id+"F26.boolean.opBoolean","COPY",FACE,{"derivedFrom":makeQuery(id+"F26.opExtrude","SWEPT_FACE",FACE,{"disambiguationData":[OSD([sQuery(id+"F25.wireOp",EDGE,"E21.left")])]})});
            var sketch = newSketch(context, id + "F27", { "sketchPlane" : qUnion([Q0])});
            skLineSegment(sketch, "E22.bottom", {"start": v(9.53, -9.53) * mm, "end": v(-9.53, -9.53) * mm});
            skLineSegment(sketch, "E22.top", {"start": v(9.53, 9.53) * mm, "end": v(-9.53, 9.53) * mm});
            skLineSegment(sketch, "E22.left", {"start": v(9.53, -9.53) * mm, "end": v(9.53, 9.53) * mm});
            skLineSegment(sketch, "E22.right", {"start": v(-9.53, -9.53) * mm, "end": v(-9.53, 9.52) * mm});
            skPoint(sketch, "E22.middle", {"position": v(0, 0) * mm});
            skLineSegment(sketch, "E23.bottom", {"start": v(-53.97, 9.53) * mm, "end": v(-73.02, 9.53) * mm});
            skLineSegment(sketch, "E23.top", {"start": v(-53.97, -9.53) * mm, "end": v(-73.02, -9.52) * mm});
            skLineSegment(sketch, "E23.left", {"start": v(-53.97, 9.53) * mm, "end": v(-53.97, -9.53) * mm});
            skLineSegment(sketch, "E23.right", {"start": v(-73.02, 9.53) * mm, "end": v(-73.02, -9.52) * mm});
            skPoint(sketch, "E23.middle", {"position": v(-63.5, 0) * mm});
            skSolve(sketch);
        }
        {
            var Q0;
            Q0 = qSketchRegion(id + "F27", true);
            extrude(context, id + "F28", {"entities" : qUnion([Q0]), "operationType" : NewBodyOperationType.REMOVE, "oppositeDirection" : true, "depth" : 12.7 * mm});
        }
    });
